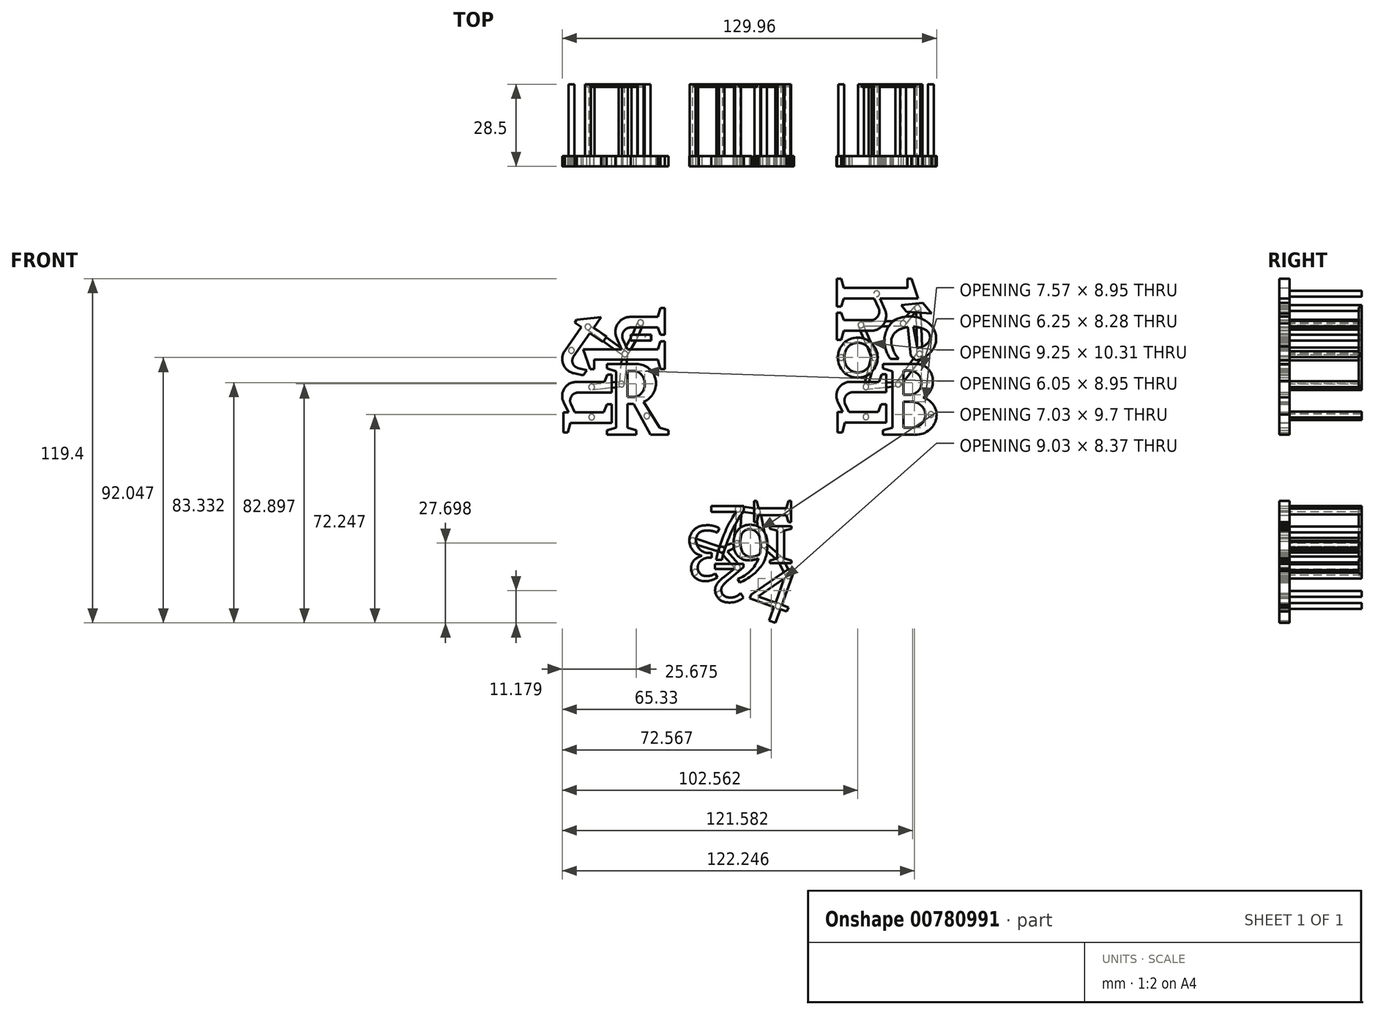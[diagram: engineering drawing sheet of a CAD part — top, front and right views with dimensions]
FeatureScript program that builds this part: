
annotation { "Feature Type Name" : "Feature", "Feature Type Description" : "" }
export const myFeature = defineFeature(function(context is Context, id is Id, definition is map)
    precondition{}
    {
        {
            var Q0;
            Q0=qCreatedBy(makeId("Front.planeOp"),FACE);
            var sketch = newSketch(context, id + "F0", { "sketchPlane" : qUnion([Q0])});
            skLineSegment(sketch, "E0", {"start": v(-78.02, 15.2) * mm, "end": v(-67.8, 15.2) * mm});
            skLineSegment(sketch, "E1", {"start": v(-67.8, 15.2) * mm, "end": v(-67.8, 16.73) * mm});
            skLineSegment(sketch, "E2", {"start": v(-67.8, 16.73) * mm, "end": v(-70.86, 17.67) * mm});
            skLineSegment(sketch, "E3", {"start": v(-70.86, 17.67) * mm, "end": v(-70.86, 25.9) * mm});
            skLineSegment(sketch, "E4", {"start": v(-70.86, 25.9) * mm, "end": v(-68.64, 25.9) * mm});
            skLineSegment(sketch, "E5", {"start": v(-68.64, 25.9) * mm, "end": v(-62.81, 15.2) * mm});
            skLineSegment(sketch, "E6", {"start": v(-62.81, 15.2) * mm, "end": v(-56.63, 15.2) * mm});
            skLineSegment(sketch, "E7", {"start": v(-56.63, 15.2) * mm, "end": v(-56.63, 16.73) * mm});
            skLineSegment(sketch, "E8", {"start": v(-56.63, 16.73) * mm, "end": v(-59.61, 17.67) * mm});
            skLineSegment(sketch, "E9", {"start": v(-59.61, 17.67) * mm, "end": v(-65.23, 26.62) * mm});
            skLineSegment(sketch, "E10", {"start": v(-78.02, 15.2) * mm, "end": v(-78.02, 16.73) * mm});
            skLineSegment(sketch, "E11", {"start": v(-78.02, 16.73) * mm, "end": v(-74.74, 17.67) * mm});
            skLineSegment(sketch, "E12", {"start": v(-74.74, 17.67) * mm, "end": v(-74.74, 37.23) * mm});
            skLineSegment(sketch, "E13", {"start": v(-74.74, 37.23) * mm, "end": v(-78.02, 38.21) * mm});
            skLineSegment(sketch, "E14", {"start": v(-78.02, 38.21) * mm, "end": v(-78.02, 39.74) * mm});
            skLineSegment(sketch, "E15", {"start": v(-78.02, 39.74) * mm, "end": v(-68.86, 39.74) * mm});
            skArc(sketch, "E16", {"start": v(-65.23, 26.62) * mm, "mid": v(-61.06, 34.23) * mm, "end": v(-67.76, 39.74) * mm});
            skArc(sketch, "E17", {"start": v(-67.74, 28.32) * mm, "mid": v(-64.81, 32.8) * mm, "end": v(-67.74, 37.27) * mm});
            skLineSegment(sketch, "E18", {"start": v(-67.74, 37.27) * mm, "end": v(-70.86, 37.27) * mm});
            skLineSegment(sketch, "E19", {"start": v(-70.86, 37.27) * mm, "end": v(-70.86, 28.32) * mm});
            skLineSegment(sketch, "E20", {"start": v(-70.86, 28.32) * mm, "end": v(-67.74, 28.32) * mm});
            skLineSegment(sketch, "E21", {"start": v(-68.86, 39.74) * mm, "end": v(-67.76, 39.74) * mm});
            skSolve(sketch);
        }
        {
            var Q0;
            Q0=makeQuery(id+"F0.imprint","IMPRINT",FACE,{"disambiguationData":[TD([[makeQuery(id+"F0.imprint","IMPRINT",EDGE,{"derivedFrom":sQuery(id+"F0.wireOp",EDGE,"E0")}),1.0]])]});
            extrude(context, id + "F1", {"entities" : qUnion([Q0]), "depth" : 3.5 * mm, "offsetDistance" : 25 * mm});
        }
        {
            var Q0;
            Q0=makeQuery(id+"F1.opExtrude","SWEPT_EDGE",EDGE,{"disambiguationData":[OSD([sQuery(id+"F0.wireOp",EDGE,"E17"),sQuery(id+"F0.wireOp",EDGE,"E18")])]});
            var Q1;
            Q1=makeQuery(id+"F1.opExtrude","SWEPT_EDGE",EDGE,{"disambiguationData":[OSD([sQuery(id+"F0.wireOp",EDGE,"E17"),sQuery(id+"F0.wireOp",EDGE,"E20")])]});
            fillet(context, id + "F2", {"entities" : qUnion([Q0, Q1]), "radius" : 3 * mm, "tangentPropagation" : true, "allowEdgeOverflow" : false});
        }
        {
            var Q0;
            Q0=qCreatedBy(makeId("Front.planeOp"),FACE);
            var sketch = newSketch(context, id + "F3", { "sketchPlane" : qUnion([Q0])});
            skLineSegment(sketch, "E22", {"start": v(-41.77, 15.2) * mm, "end": v(-34.7, 15.2) * mm});
            skLineSegment(sketch, "E23", {"start": v(-34.7, 15.2) * mm, "end": v(-34.7, 16.73) * mm});
            skLineSegment(sketch, "E24", {"start": v(-34.7, 16.73) * mm, "end": v(-38.08, 17.67) * mm});
            skLineSegment(sketch, "E25", {"start": v(-38.08, 17.67) * mm, "end": v(-38.08, 32) * mm});
            skLineSegment(sketch, "E26", {"start": v(-38.08, 32) * mm, "end": v(-44.47, 32) * mm});
            skLineSegment(sketch, "E27", {"start": v(-44.47, 32) * mm, "end": v(-44.47, 30.27) * mm});
            skLineSegment(sketch, "E28", {"start": v(-44.47, 30.27) * mm, "end": v(-41.77, 29.18) * mm});
            skLineSegment(sketch, "E29", {"start": v(-41.77, 29.18) * mm, "end": v(-41.77, 19.11) * mm});
            skLineSegment(sketch, "E30", {"start": v(-41.77, 15.2) * mm, "end": v(-41.77, 16.98) * mm});
            skLineSegment(sketch, "E31", {"start": v(-41.77, 16.98) * mm, "end": v(-45.17, 15.3) * mm});
            skLineSegment(sketch, "E32", {"start": v(-41.77, 19.11) * mm, "end": v(-44.76, 17.72) * mm});
            skLineSegment(sketch, "E33", {"start": v(-52.26, 19.48) * mm, "end": v(-52.26, 29.48) * mm});
            skLineSegment(sketch, "E34", {"start": v(-52.26, 29.48) * mm, "end": v(-54.82, 30.46) * mm});
            skLineSegment(sketch, "E35", {"start": v(-54.82, 30.46) * mm, "end": v(-54.82, 32) * mm});
            skLineSegment(sketch, "E36", {"start": v(-54.82, 32) * mm, "end": v(-48.6, 32) * mm});
            skLineSegment(sketch, "E37", {"start": v(-48.6, 32) * mm, "end": v(-48.6, 20.2) * mm});
            skArc(sketch, "E38", {"start": v(-52.26, 19.48) * mm, "mid": v(-49.87, 15.44) * mm, "end": v(-45.17, 15.3) * mm});
            skArc(sketch, "E39", {"start": v(-48.6, 20.2) * mm, "mid": v(-47.31, 17.98) * mm, "end": v(-44.76, 17.72) * mm});
            skSolve(sketch);
        }
        {
            var Q0;
            Q0=makeQuery(id+"F3.imprint","IMPRINT",FACE,{"disambiguationData":[TD([[makeQuery(id+"F3.imprint","IMPRINT",EDGE,{"derivedFrom":sQuery(id+"F3.wireOp",EDGE,"E22")}),1.0]])]});
            extrude(context, id + "F4", {"entities" : qUnion([Q0]), "depth" : 3.5 * mm, "offsetDistance" : 25 * mm});
        }
        {
            var Q0;
            Q0=qCreatedBy(makeId("Front.planeOp"),FACE);
            var sketch = newSketch(context, id + "F5", { "sketchPlane" : qUnion([Q0])});
            skLineSegment(sketch, "E40", {"start": v(-20.57, 32) * mm, "end": v(-26.02, 32) * mm});
            skLineSegment(sketch, "E41", {"start": v(-26.02, 32) * mm, "end": v(-26.02, 36.51) * mm});
            skLineSegment(sketch, "E42", {"start": v(-26.02, 36.51) * mm, "end": v(-32.46, 30.8) * mm});
            skLineSegment(sketch, "E43", {"start": v(-32.46, 30.8) * mm, "end": v(-32.46, 29.66) * mm});
            skLineSegment(sketch, "E44", {"start": v(-32.46, 29.66) * mm, "end": v(-29.69, 29.66) * mm});
            skLineSegment(sketch, "E45", {"start": v(-29.69, 29.66) * mm, "end": v(-29.69, 19.66) * mm});
            skLineSegment(sketch, "E46", {"start": v(-20.57, 32) * mm, "end": v(-20.57, 29.66) * mm});
            skLineSegment(sketch, "E47", {"start": v(-20.57, 29.66) * mm, "end": v(-26.02, 29.66) * mm});
            skLineSegment(sketch, "E48", {"start": v(-26.02, 29.66) * mm, "end": v(-26.02, 19.66) * mm});
            skLineSegment(sketch, "E49", {"start": v(-22.55, 17.37) * mm, "end": v(-19.53, 18.45) * mm});
            skLineSegment(sketch, "E50", {"start": v(-19.53, 18.45) * mm, "end": v(-19.53, 16.4) * mm});
            skLineSegment(sketch, "E51", {"start": v(-19.53, 16.4) * mm, "end": v(-22.56, 15.09) * mm});
            skArc(sketch, "E52", {"start": v(-29.69, 19.66) * mm, "mid": v(-27.34, 15.48) * mm, "end": v(-22.56, 15.09) * mm});
            skArc(sketch, "E53", {"start": v(-26.02, 19.66) * mm, "mid": v(-24.85, 17.65) * mm, "end": v(-22.55, 17.37) * mm});
            skSolve(sketch);
        }
        {
            var Q0;
            Q0=makeQuery(id+"F5.imprint","IMPRINT",FACE,{"disambiguationData":[TD([[makeQuery(id+"F5.imprint","IMPRINT",EDGE,{"derivedFrom":sQuery(id+"F5.wireOp",EDGE,"E40")}),1.0]])]});
            extrude(context, id + "F6", {"entities" : qUnion([Q0]), "depth" : 3.5 * mm, "offsetDistance" : 25 * mm});
        }
        {
            var Q0;
            Q0=qCreatedBy(makeId("Front.planeOp"),FACE);
            var sketch = newSketch(context, id + "F7", { "sketchPlane" : qUnion([Q0])});
            skLineSegment(sketch, "E54", {"start": v(-17.06, 15.2) * mm, "end": v(-7.42, 15.2) * mm});
            skLineSegment(sketch, "E55", {"start": v(-7.42, 15.2) * mm, "end": v(-7.42, 16.73) * mm});
            skLineSegment(sketch, "E56", {"start": v(-7.42, 16.73) * mm, "end": v(-10.26, 17.67) * mm});
            skLineSegment(sketch, "E57", {"start": v(-10.26, 17.67) * mm, "end": v(-10.26, 28.2) * mm});
            skLineSegment(sketch, "E58", {"start": v(-10.26, 28.2) * mm, "end": v(-6.9, 29.76) * mm});
            skLineSegment(sketch, "E59", {"start": v(-17.06, 15.2) * mm, "end": v(-17.06, 16.73) * mm});
            skLineSegment(sketch, "E60", {"start": v(-17.06, 16.73) * mm, "end": v(-13.88, 17.67) * mm});
            skLineSegment(sketch, "E61", {"start": v(-13.88, 17.67) * mm, "end": v(-13.88, 39.74) * mm});
            skLineSegment(sketch, "E62", {"start": v(-13.88, 39.74) * mm, "end": v(-17.06, 39.74) * mm});
            skLineSegment(sketch, "E63", {"start": v(-17.06, 39.74) * mm, "end": v(-17.06, 41.1) * mm});
            skLineSegment(sketch, "E64", {"start": v(-17.06, 41.1) * mm, "end": v(-10.26, 43.5) * mm});
            skLineSegment(sketch, "E65", {"start": v(-10.26, 43.5) * mm, "end": v(-10.26, 30.24) * mm});
            skLineSegment(sketch, "E66", {"start": v(-10.26, 30.24) * mm, "end": v(-6.4, 31.9) * mm});
            skLineSegment(sketch, "E67", {"start": v(-2.67, 27.17) * mm, "end": v(-2.67, 17.67) * mm});
            skLineSegment(sketch, "E68", {"start": v(-2.67, 17.67) * mm, "end": v(-5.22, 16.73) * mm});
            skLineSegment(sketch, "E69", {"start": v(-5.22, 16.73) * mm, "end": v(-5.22, 15.2) * mm});
            skLineSegment(sketch, "E70", {"start": v(-5.22, 15.2) * mm, "end": v(4.1, 15.2) * mm});
            skLineSegment(sketch, "E71", {"start": v(4.1, 15.2) * mm, "end": v(4.1, 16.73) * mm});
            skLineSegment(sketch, "E72", {"start": v(4.1, 16.73) * mm, "end": v(0.99, 17.67) * mm});
            skLineSegment(sketch, "E73", {"start": v(0.99, 17.67) * mm, "end": v(0.99, 27.07) * mm});
            skArc(sketch, "E74", {"start": v(0.99, 27.07) * mm, "mid": v(-1.37, 31.53) * mm, "end": v(-6.4, 31.9) * mm});
            skArc(sketch, "E75", {"start": v(-2.67, 27.17) * mm, "mid": v(-4.12, 29.56) * mm, "end": v(-6.9, 29.76) * mm});
            skSolve(sketch);
        }
        {
            var Q0;
            Q0=makeQuery(id+"F7.imprint","IMPRINT",FACE,{"disambiguationData":[TD([[makeQuery(id+"F7.imprint","IMPRINT",EDGE,{"derivedFrom":sQuery(id+"F7.wireOp",EDGE,"E54")}),1.0]])]});
            extrude(context, id + "F8", {"entities" : qUnion([Q0]), "depth" : 3.5 * mm, "offsetDistance" : 25 * mm});
        }
        {
            var Q0;
            Q0=qCreatedBy(makeId("Front.planeOp"),FACE);
            var sketch = newSketch(context, id + "F9", { "sketchPlane" : qUnion([Q0])});
            skLineSegment(sketch, "E76", {"start": v(29.79, 15.2) * mm, "end": v(17.79, 15.2) * mm});
            skLineSegment(sketch, "E77", {"start": v(17.79, 15.2) * mm, "end": v(17.79, 16.73) * mm});
            skLineSegment(sketch, "E78", {"start": v(17.79, 16.73) * mm, "end": v(21.07, 17.67) * mm});
            skLineSegment(sketch, "E79", {"start": v(21.07, 17.67) * mm, "end": v(21.07, 37.23) * mm});
            skLineSegment(sketch, "E80", {"start": v(21.07, 37.23) * mm, "end": v(17.79, 38.21) * mm});
            skLineSegment(sketch, "E81", {"start": v(17.79, 38.21) * mm, "end": v(17.79, 39.74) * mm});
            skLineSegment(sketch, "E82", {"start": v(17.79, 39.74) * mm, "end": v(29.42, 39.74) * mm});
            skLineSegment(sketch, "E83", {"start": v(27.65, 37.37) * mm, "end": v(24.95, 37.37) * mm});
            skLineSegment(sketch, "E84", {"start": v(24.95, 37.37) * mm, "end": v(24.95, 29.1) * mm});
            skLineSegment(sketch, "E85", {"start": v(24.95, 29.1) * mm, "end": v(27.65, 29.1) * mm});
            skLineSegment(sketch, "E86", {"start": v(27.84, 26.62) * mm, "end": v(24.95, 26.62) * mm});
            skLineSegment(sketch, "E87", {"start": v(24.95, 26.62) * mm, "end": v(24.95, 17.67) * mm});
            skLineSegment(sketch, "E88", {"start": v(24.95, 17.67) * mm, "end": v(28.14, 17.67) * mm});
            skArc(sketch, "E89", {"start": v(35.13, 33.82) * mm, "mid": v(33.53, 38) * mm, "end": v(29.42, 39.74) * mm});
            skArc(sketch, "E90", {"start": v(31.72, 28.11) * mm, "mid": v(34.29, 30.45) * mm, "end": v(35.13, 33.82) * mm});
            skArc(sketch, "E91", {"start": v(36.45, 22.2) * mm, "mid": v(35.03, 25.92) * mm, "end": v(31.72, 28.11) * mm});
            skArc(sketch, "E92", {"start": v(29.79, 15.2) * mm, "mid": v(34.49, 17.4) * mm, "end": v(36.45, 22.2) * mm});
            skArc(sketch, "E93", {"start": v(32.52, 22.31) * mm, "mid": v(31.02, 25.38) * mm, "end": v(27.84, 26.62) * mm});
            skArc(sketch, "E94", {"start": v(28.14, 17.67) * mm, "mid": v(31.33, 19.05) * mm, "end": v(32.52, 22.31) * mm});
            skArc(sketch, "E95", {"start": v(27.65, 29.1) * mm, "mid": v(31.2, 33.23) * mm, "end": v(27.65, 37.37) * mm});
            skSolve(sketch);
        }
        {
            var Q0;
            Q0=makeQuery(id+"F9.imprint","IMPRINT",FACE,{"disambiguationData":[TD([[makeQuery(id+"F9.imprint","IMPRINT",EDGE,{"derivedFrom":sQuery(id+"F9.wireOp",EDGE,"E76")}),-1.0]])]});
            extrude(context, id + "F10", {"entities" : qUnion([Q0]), "depth" : 3.5 * mm, "offsetDistance" : 25 * mm});
        }
        {
            var Q0;
            Q0=makeQuery(id+"F10.opExtrude","SWEPT_EDGE",EDGE,{"disambiguationData":[OSD([sQuery(id+"F9.wireOp",EDGE,"E83"),sQuery(id+"F9.wireOp",EDGE,"E95")])]});
            var Q1;
            Q1=makeQuery(id+"F10.opExtrude","SWEPT_EDGE",EDGE,{"disambiguationData":[OSD([sQuery(id+"F9.wireOp",EDGE,"E85"),sQuery(id+"F9.wireOp",EDGE,"E95")])]});
            fillet(context, id + "F11", {"entities" : qUnion([Q0, Q1]), "radius" : 3 * mm, "tangentPropagation" : true, "allowEdgeOverflow" : false});
        }
        {
            var Q0;
            Q0=qCreatedBy(makeId("Front.planeOp"),FACE);
            var sketch = newSketch(context, id + "F12", { "sketchPlane" : qUnion([Q0])});
            skLineSegment(sketch, "E96", {"start": v(90.8, 34.88) * mm, "end": v(93.74, 34.88) * mm});
            skLineSegment(sketch, "E97", {"start": v(93.74, 34.88) * mm, "end": v(99.81, 41.18) * mm});
            skLineSegment(sketch, "E98", {"start": v(99.81, 41.18) * mm, "end": v(95.06, 41.18) * mm});
            skLineSegment(sketch, "E99", {"start": v(95.06, 41.18) * mm, "end": v(90.8, 34.88) * mm});
            skLineSegment(sketch, "E100", {"start": v(99.7, 23.95) * mm, "end": v(101.36, 25.66) * mm});
            skArc(sketch, "E101", {"start": v(101.36, 25.66) * mm, "mid": v(99.76, 29.5) * mm, "end": v(96.55, 32.12) * mm});
            skArc(sketch, "E102", {"start": v(96.55, 32.12) * mm, "mid": v(92.2, 32.52) * mm, "end": v(88.49, 30.24) * mm});
            skArc(sketch, "E103", {"start": v(88.49, 30.24) * mm, "mid": v(86.13, 24.18) * mm, "end": v(87.72, 17.87) * mm});
            skArc(sketch, "E104", {"start": v(87.72, 17.87) * mm, "mid": v(91.03, 15.46) * mm, "end": v(95.06, 14.72) * mm});
            skArc(sketch, "E105", {"start": v(95.06, 14.72) * mm, "mid": v(98.1, 15.4) * mm, "end": v(100.86, 16.82) * mm});
            skLineSegment(sketch, "E106", {"start": v(100.86, 16.82) * mm, "end": v(100.86, 19.7) * mm});
            skArc(sketch, "E107", {"start": v(94.95, 17.1) * mm, "mid": v(98.11, 17.92) * mm, "end": v(100.86, 19.7) * mm});
            skArc(sketch, "E108", {"start": v(90.8, 19.7) * mm, "mid": v(92.53, 17.83) * mm, "end": v(94.95, 17.1) * mm});
            skArc(sketch, "E109", {"start": v(90.8, 29.14) * mm, "mid": v(89.98, 26.84) * mm, "end": v(89.7, 24.42) * mm});
            skArc(sketch, "E110", {"start": v(95.94, 29.14) * mm, "mid": v(93.38, 30.56) * mm, "end": v(90.8, 29.14) * mm});
            skArc(sketch, "E111", {"start": v(97.1, 26.21) * mm, "mid": v(96.68, 27.74) * mm, "end": v(95.94, 29.14) * mm});
            skLineSegment(sketch, "E112", {"start": v(99.7, 23.95) * mm, "end": v(89.81, 22.85) * mm});
            skLineSegment(sketch, "E113", {"start": v(97.1, 26.21) * mm, "end": v(89.7, 24.76) * mm});
            skPoint(sketch, "E113.endSnap0", {"position": v(89.7, 24.42) * mm});
            skArc(sketch, "E114.trimOffspring", {"start": v(89.81, 22.85) * mm, "mid": v(90.19, 21.23) * mm, "end": v(90.8, 19.7) * mm});
            skPoint(sketch, "E115.orphan", {"position": v(87.94, 24.42) * mm});
            skSolve(sketch);
        }
        {
            var Q0;
            Q0=makeQuery(id+"F12.imprint","IMPRINT",FACE,{"disambiguationData":[TD([[makeQuery(id+"F12.imprint","IMPRINT",EDGE,{"derivedFrom":sQuery(id+"F12.wireOp",EDGE,"E100")}),1.0]])]});
            var Q1;
            Q1=makeQuery(id+"F12.imprint","IMPRINT",FACE,{"disambiguationData":[TD([[makeQuery(id+"F12.imprint","IMPRINT",EDGE,{"derivedFrom":sQuery(id+"F12.wireOp",EDGE,"E96")}),1.0]])]});
            extrude(context, id + "F13", {"entities" : qUnion([Q0, Q1]), "depth" : 3.5 * mm, "offsetDistance" : 25 * mm});
        }
        {
            var Q0;
            Q0=makeQuery(id+"F4.opExtrude","SWEPT_BODY",BODY,{"disambiguationData":[OSD([sQuery(id+"F3.wireOp",EDGE,"E22"),sQuery(id+"F3.wireOp",EDGE,"E23"),sQuery(id+"F3.wireOp",EDGE,"E24"),sQuery(id+"F3.wireOp",EDGE,"E25"),sQuery(id+"F3.wireOp",EDGE,"E26"),sQuery(id+"F3.wireOp",EDGE,"E27"),sQuery(id+"F3.wireOp",EDGE,"E28"),sQuery(id+"F3.wireOp",EDGE,"E29"),sQuery(id+"F3.wireOp",EDGE,"E30"),sQuery(id+"F3.wireOp",EDGE,"E31"),sQuery(id+"F3.wireOp",EDGE,"E32"),sQuery(id+"F3.wireOp",EDGE,"E33"),sQuery(id+"F3.wireOp",EDGE,"E34"),sQuery(id+"F3.wireOp",EDGE,"E35"),sQuery(id+"F3.wireOp",EDGE,"E36"),sQuery(id+"F3.wireOp",EDGE,"E37"),sQuery(id+"F3.wireOp",EDGE,"E38"),sQuery(id+"F3.wireOp",EDGE,"E39")])]});
            transform(context, id + "F14", {"entities" : qUnion([Q0]), "transformType" : TransformType.TRANSLATION_3D, "dx" : 94.3 * mm, "dy" : 0 * mm, "dz" : 0 * mm, "makeCopy" : true});
        }
        {
            var Q0;
            Q0=makeQuery(id+"F8.opExtrude","SWEPT_BODY",BODY,{"disambiguationData":[OSD([sQuery(id+"F7.wireOp",EDGE,"E54"),sQuery(id+"F7.wireOp",EDGE,"E55"),sQuery(id+"F7.wireOp",EDGE,"E56"),sQuery(id+"F7.wireOp",EDGE,"E57"),sQuery(id+"F7.wireOp",EDGE,"E58"),sQuery(id+"F7.wireOp",EDGE,"E59"),sQuery(id+"F7.wireOp",EDGE,"E60"),sQuery(id+"F7.wireOp",EDGE,"E61"),sQuery(id+"F7.wireOp",EDGE,"E62"),sQuery(id+"F7.wireOp",EDGE,"E63"),sQuery(id+"F7.wireOp",EDGE,"E64"),sQuery(id+"F7.wireOp",EDGE,"E65"),sQuery(id+"F7.wireOp",EDGE,"E66"),sQuery(id+"F7.wireOp",EDGE,"E67"),sQuery(id+"F7.wireOp",EDGE,"E68"),sQuery(id+"F7.wireOp",EDGE,"E69"),sQuery(id+"F7.wireOp",EDGE,"E70"),sQuery(id+"F7.wireOp",EDGE,"E71"),sQuery(id+"F7.wireOp",EDGE,"E72"),sQuery(id+"F7.wireOp",EDGE,"E73"),sQuery(id+"F7.wireOp",EDGE,"E74"),sQuery(id+"F7.wireOp",EDGE,"E75")])]});
            transform(context, id + "F15", {"entities" : qUnion([Q0]), "transformType" : TransformType.TRANSLATION_3D, "dx" : 79.7 * mm, "dy" : 0 * mm, "dz" : 0 * mm, "makeCopy" : true});
        }
        {
            var Q0;
            Q0=qCreatedBy(makeId("Front.planeOp"),FACE);
            var sketch = newSketch(context, id + "F16", { "sketchPlane" : qUnion([Q0])});
            skLineSegment(sketch, "E116", {"start": v(-44.04, -29.35) * mm, "end": v(-36.6, -29.35) * mm});
            skLineSegment(sketch, "E117", {"start": v(-36.6, -29.35) * mm, "end": v(-36.6, -28.47) * mm});
            skLineSegment(sketch, "E118", {"start": v(-36.6, -28.47) * mm, "end": v(-39.1, -27.72) * mm});
            skLineSegment(sketch, "E119", {"start": v(-39.1, -27.72) * mm, "end": v(-39.1, -18.13) * mm});
            skLineSegment(sketch, "E120", {"start": v(-39.1, -18.13) * mm, "end": v(-36.6, -17.38) * mm});
            skLineSegment(sketch, "E121", {"start": v(-36.6, -17.38) * mm, "end": v(-36.6, -16.5) * mm});
            skLineSegment(sketch, "E122", {"start": v(-36.6, -16.5) * mm, "end": v(-44.04, -16.5) * mm});
            skLineSegment(sketch, "E123", {"start": v(-44.04, -16.5) * mm, "end": v(-44.04, -17.38) * mm});
            skLineSegment(sketch, "E124", {"start": v(-44.04, -17.38) * mm, "end": v(-41.53, -18.13) * mm});
            skLineSegment(sketch, "E125", {"start": v(-41.53, -18.13) * mm, "end": v(-41.53, -27.72) * mm});
            skLineSegment(sketch, "E126", {"start": v(-41.53, -27.72) * mm, "end": v(-44.04, -28.47) * mm});
            skLineSegment(sketch, "E127", {"start": v(-44.04, -28.47) * mm, "end": v(-44.04, -29.35) * mm});
            skSolve(sketch);
        }
        {
            var Q0;
            Q0=makeQuery(id+"F16.imprint","IMPRINT",FACE,{"disambiguationData":[TD([[makeQuery(id+"F16.imprint","IMPRINT",EDGE,{"derivedFrom":sQuery(id+"F16.wireOp",EDGE,"E116")}),1.0]])]});
            extrude(context, id + "F17", {"entities" : qUnion([Q0]), "depth" : 3.5 * mm, "offsetDistance" : 25 * mm});
        }
        {
            var Q0;
            Q0=makeQuery(id+"F17.opExtrude","SWEPT_BODY",BODY,{"disambiguationData":[OSD([sQuery(id+"F16.wireOp",EDGE,"E116"),sQuery(id+"F16.wireOp",EDGE,"E117"),sQuery(id+"F16.wireOp",EDGE,"E118"),sQuery(id+"F16.wireOp",EDGE,"E119"),sQuery(id+"F16.wireOp",EDGE,"E120"),sQuery(id+"F16.wireOp",EDGE,"E121"),sQuery(id+"F16.wireOp",EDGE,"E122"),sQuery(id+"F16.wireOp",EDGE,"E123"),sQuery(id+"F16.wireOp",EDGE,"E124"),sQuery(id+"F16.wireOp",EDGE,"E125"),sQuery(id+"F16.wireOp",EDGE,"E126"),sQuery(id+"F16.wireOp",EDGE,"E127")])]});
            transform(context, id + "F18", {"entities" : qUnion([Q0]), "transformType" : TransformType.TRANSLATION_3D, "dx" : 104.3 * mm, "dy" : 0 * mm, "dz" : 0 * mm, "makeCopy" : true});
        }
        {
            var Q0;
            Q0=qCreatedBy(makeId("Front.planeOp"),FACE);
            var sketch = newSketch(context, id + "F19", { "sketchPlane" : qUnion([Q0])});
            skLineSegment(sketch, "E128", {"start": v(3.98, -15.35) * mm, "end": v(3.98, -27.8) * mm});
            skLineSegment(sketch, "E129", {"start": v(3.98, -34.4) * mm, "end": v(1.63, -34.4) * mm});
            skLineSegment(sketch, "E130", {"start": v(1.63, -34.4) * mm, "end": v(1.63, -29.38) * mm});
            skLineSegment(sketch, "E131", {"start": v(1.63, -18.9) * mm, "end": v(-4.74, -27.8) * mm});
            skLineSegment(sketch, "E132", {"start": v(-4.74, -27.8) * mm, "end": v(1.63, -27.8) * mm});
            skLineSegment(sketch, "E133", {"start": v(6.36, -27.8) * mm, "end": v(6.36, -29.38) * mm});
            skLineSegment(sketch, "E134", {"start": v(6.36, -29.38) * mm, "end": v(3.98, -29.38) * mm});
            skLineSegment(sketch, "E135", {"start": v(-7.27, -29.38) * mm, "end": v(-7.27, -28.07) * mm});
            skLineSegment(sketch, "E136", {"start": v(-7.27, -28.07) * mm, "end": v(1.83, -15.35) * mm});
            skLineSegment(sketch, "E137", {"start": v(1.83, -15.35) * mm, "end": v(3.98, -15.35) * mm});
            skLineSegment(sketch, "E138.trimOffspring", {"start": v(3.98, -27.8) * mm, "end": v(6.36, -27.8) * mm});
            skLineSegment(sketch, "E139.trimOffspring", {"start": v(1.63, -29.38) * mm, "end": v(-7.27, -29.38) * mm});
            skLineSegment(sketch, "E140.trimOffspring", {"start": v(1.63, -27.8) * mm, "end": v(1.63, -18.9) * mm});
            skLineSegment(sketch, "E141.trimOffspring", {"start": v(3.98, -29.38) * mm, "end": v(3.98, -34.4) * mm});
            skSolve(sketch);
        }
        {
            var Q0;
            Q0=makeQuery(id+"F19.imprint","IMPRINT",FACE,{"disambiguationData":[TD([[makeQuery(id+"F19.imprint","IMPRINT",EDGE,{"derivedFrom":sQuery(id+"F19.wireOp",EDGE,"E128")}),-1.0]])]});
            extrude(context, id + "F20", {"entities" : qUnion([Q0]), "depth" : 3.5 * mm, "offsetDistance" : 25 * mm});
        }
        {
            var Q0;
            Q0=qCreatedBy(makeId("Front.planeOp"),FACE);
            var sketch = newSketch(context, id + "F21", { "sketchPlane" : qUnion([Q0])});
            skLineSegment(sketch, "E142", {"start": v(77.45, -18.55) * mm, "end": v(68.9, -18.55) * mm});
            skLineSegment(sketch, "E143", {"start": v(68.9, -18.55) * mm, "end": v(68.9, -16.5) * mm});
            skLineSegment(sketch, "E144", {"start": v(68.9, -16.5) * mm, "end": v(80.12, -16.5) * mm});
            skLineSegment(sketch, "E145", {"start": v(80.12, -16.5) * mm, "end": v(80.12, -18.07) * mm});
            skLineSegment(sketch, "E146", {"start": v(70.5, -35.3) * mm, "end": v(72.5, -35.3) * mm});
            skArc(sketch, "E147", {"start": v(77.45, -18.55) * mm, "mid": v(73.16, -26.58) * mm, "end": v(70.5, -35.3) * mm});
            skArc(sketch, "E148", {"start": v(80.12, -18.07) * mm, "mid": v(75.5, -26.32) * mm, "end": v(72.5, -35.3) * mm});
            skSolve(sketch);
        }
        {
            var Q0;
            Q0=makeQuery(id+"F21.imprint","IMPRINT",FACE,{"disambiguationData":[TD([[makeQuery(id+"F21.imprint","IMPRINT",EDGE,{"derivedFrom":sQuery(id+"F21.wireOp",EDGE,"E142")}),-1.0]])]});
            extrude(context, id + "F22", {"entities" : qUnion([Q0]), "depth" : 3.5 * mm, "offsetDistance" : 25 * mm});
        }
        {
            var Q0;
            Q0=qCreatedBy(makeId("Front.planeOp"),FACE);
            var sketch = newSketch(context, id + "F23", { "sketchPlane" : qUnion([Q0])});
            skCircle(sketch, "E149", {"center": v(51.05, -22.75) * mm, "radius": 6.94 * mm});
            skPoint(sketch, "E149.first.point", {"position": v(51, -15.8) * mm});
            skPoint(sketch, "E149.second.point", {"position": v(45.69, -27.17) * mm});
            skPoint(sketch, "E149.third.point", {"position": v(55.6, -28) * mm});
            skArc(sketch, "E150", {"start": v(55.13, -20.1) * mm, "mid": v(51.07, -17.6) * mm, "end": v(47, -20.1) * mm});
            skArc(sketch, "E151", {"start": v(55.13, -25.4) * mm, "mid": v(55.68, -22.75) * mm, "end": v(55.13, -20.1) * mm});
            skArc(sketch, "E152", {"start": v(47, -25.4) * mm, "mid": v(51.07, -27.9) * mm, "end": v(55.13, -25.4) * mm});
            skArc(sketch, "E153", {"start": v(47, -20.1) * mm, "mid": v(46.43, -22.75) * mm, "end": v(47, -25.4) * mm});
            skSolve(sketch);
        }
        {
            var Q0;
            Q0=makeQuery(id+"F23.imprint","IMPRINT",FACE,{"disambiguationData":[TD([[makeQuery(id+"F23.imprint","IMPRINT",EDGE,{"derivedFrom":sQuery(id+"F23.wireOp",EDGE,"E149")}),1.0]])]});
            extrude(context, id + "F24", {"entities" : qUnion([Q0]), "depth" : 3.5 * mm, "offsetDistance" : 25 * mm});
        }
        {
            var Q0;
            Q0=qCreatedBy(makeId("Front.planeOp"),FACE);
            var sketch = newSketch(context, id + "F25", { "sketchPlane" : qUnion([Q0])});
            skLineSegment(sketch, "E154", {"start": v(-32.6, -34.83) * mm, "end": v(-31.92, -36.07) * mm});
            skArc(sketch, "E155", {"start": v(-31.92, -36.07) * mm, "mid": v(-27.4, -33.47) * mm, "end": v(-23.88, -29.64) * mm});
            skArc(sketch, "E156", {"start": v(-23.88, -29.64) * mm, "mid": v(-22.4, -25.11) * mm, "end": v(-22.58, -20.35) * mm});
            skArc(sketch, "E157", {"start": v(-22.58, -20.35) * mm, "mid": v(-24.48, -17.39) * mm, "end": v(-27.75, -16.08) * mm});
            skArc(sketch, "E158", {"start": v(-27.75, -16.08) * mm, "mid": v(-31.59, -17.06) * mm, "end": v(-33.8, -20.35) * mm});
            skArc(sketch, "E159", {"start": v(-33.8, -20.35) * mm, "mid": v(-34.09, -22.6) * mm, "end": v(-33.8, -24.86) * mm});
            skArc(sketch, "E160", {"start": v(-33.8, -24.86) * mm, "mid": v(-32.49, -26.9) * mm, "end": v(-30.42, -28.18) * mm});
            skArc(sketch, "E161", {"start": v(-30.42, -28.18) * mm, "mid": v(-27.86, -28.35) * mm, "end": v(-25.36, -27.73) * mm});
            skArc(sketch, "E162", {"start": v(-32.6, -34.83) * mm, "mid": v(-28.19, -32.08) * mm, "end": v(-25.36, -27.73) * mm});
            skArc(sketch, "E163", {"start": v(-24.9, -26.21) * mm, "mid": v(-24.66, -23.55) * mm, "end": v(-24.9, -20.88) * mm});
            skArc(sketch, "E164", {"start": v(-24.9, -20.88) * mm, "mid": v(-25.91, -18.76) * mm, "end": v(-27.94, -17.58) * mm});
            skPoint(sketch, "E165", {"position": v(-34.09, -22.6) * mm});
            skPoint(sketch, "E166", {"position": v(-31.68, -22.64) * mm});
            skArc(sketch, "E167", {"start": v(-27.94, -17.58) * mm, "mid": v(-30, -18) * mm, "end": v(-31.34, -19.63) * mm});
            skArc(sketch, "E168", {"start": v(-31.34, -19.63) * mm, "mid": v(-31.68, -22.61) * mm, "end": v(-30.95, -25.53) * mm});
            skArc(sketch, "E169", {"start": v(-30.95, -25.53) * mm, "mid": v(-29.66, -26.77) * mm, "end": v(-27.94, -27.25) * mm});
            skArc(sketch, "E170", {"start": v(-27.94, -27.25) * mm, "mid": v(-26.37, -26.95) * mm, "end": v(-24.92, -26.27) * mm});
            skArc(sketch, "E171.trimOffspring", {"start": v(-24.92, -26.27) * mm, "mid": v(-24.91, -26.24) * mm, "end": v(-24.9, -26.21) * mm});
            skPoint(sketch, "E172.orphan", {"position": v(-23.96, -25.53) * mm});
            skSolve(sketch);
        }
        {
            var Q0;
            Q0=makeQuery(id+"F25.imprint","IMPRINT",FACE,{"disambiguationData":[TD([[makeQuery(id+"F25.imprint","IMPRINT",EDGE,{"derivedFrom":sQuery(id+"F25.wireOp",EDGE,"E154")}),1.0]])]});
            extrude(context, id + "F26", {"entities" : qUnion([Q0]), "depth" : 3.5 * mm, "offsetDistance" : 25 * mm});
        }
        {
            var Q0;
            Q0=qCreatedBy(makeId("Front.planeOp"),FACE);
            var sketch = newSketch(context, id + "F27", { "sketchPlane" : qUnion([Q0])});
            skLineSegment(sketch, "E173", {"start": v(-19.06, -17.35) * mm, "end": v(-18.22, -18.65) * mm});
            skLineSegment(sketch, "E174", {"start": v(-17.14, -24.16) * mm, "end": v(-17.14, -25.79) * mm});
            skLineSegment(sketch, "E175", {"start": v(-19.06, -32.87) * mm, "end": v(-19.75, -34.37) * mm});
            skArc(sketch, "E176", {"start": v(-12.61, -16.41) * mm, "mid": v(-15.95, -16.09) * mm, "end": v(-19.06, -17.35) * mm});
            skArc(sketch, "E177", {"start": v(-10.6, -22.78) * mm, "mid": v(-10.12, -19.12) * mm, "end": v(-12.61, -16.41) * mm});
            skArc(sketch, "E178", {"start": v(-13.75, -24.8) * mm, "mid": v(-11.98, -24.08) * mm, "end": v(-10.6, -22.78) * mm});
            skArc(sketch, "E179", {"start": v(-19.75, -34.37) * mm, "mid": v(-16.24, -35.41) * mm, "end": v(-12.61, -34.9) * mm});
            skArc(sketch, "E180", {"start": v(-12.61, -34.9) * mm, "mid": v(-9.5, -31.3) * mm, "end": v(-10.6, -26.67) * mm});
            skArc(sketch, "E181", {"start": v(-10.6, -26.67) * mm, "mid": v(-12, -25.43) * mm, "end": v(-13.75, -24.8) * mm});
            skArc(sketch, "E182", {"start": v(-13.75, -18.1) * mm, "mid": v(-16.05, -17.8) * mm, "end": v(-18.22, -18.65) * mm});
            skArc(sketch, "E183", {"start": v(-13.75, -23.42) * mm, "mid": v(-12.26, -20.76) * mm, "end": v(-13.75, -18.1) * mm});
            skLineSegment(sketch, "E184", {"start": v(-17.14, -24.16) * mm, "end": v(-16.1, -24.16) * mm});
            skLineSegment(sketch, "E185", {"start": v(-17.14, -25.79) * mm, "end": v(-16.1, -25.79) * mm});
            skArc(sketch, "E186", {"start": v(-16.1, -24.16) * mm, "mid": v(-14.87, -23.97) * mm, "end": v(-13.75, -23.42) * mm});
            skArc(sketch, "E187", {"start": v(-11.68, -29.94) * mm, "mid": v(-13.07, -26.99) * mm, "end": v(-16.1, -25.79) * mm});
            skArc(sketch, "E188", {"start": v(-19.06, -32.87) * mm, "mid": v(-16.72, -33.52) * mm, "end": v(-14.29, -33.48) * mm});
            skArc(sketch, "E189", {"start": v(-14.29, -33.48) * mm, "mid": v(-12.26, -32.25) * mm, "end": v(-11.68, -29.94) * mm});
            skSolve(sketch);
        }
        {
            var Q0;
            Q0=makeQuery(id+"F27.imprint","IMPRINT",FACE,{"disambiguationData":[TD([[makeQuery(id+"F27.imprint","IMPRINT",EDGE,{"derivedFrom":sQuery(id+"F27.wireOp",EDGE,"E173")}),1.0]])]});
            extrude(context, id + "F28", {"entities" : qUnion([Q0]), "depth" : 3.5 * mm, "offsetDistance" : 25 * mm});
        }
        {
            var Q0;
            Q0=qCreatedBy(makeId("Front.planeOp"),FACE);
            var sketch = newSketch(context, id + "F29", { "sketchPlane" : qUnion([Q0])});
            skLineSegment(sketch, "E190.bottom", {"start": v(14.61, -21.22) * mm, "end": v(21.72, -21.22) * mm});
            skLineSegment(sketch, "E190.top", {"start": v(14.61, -23.3) * mm, "end": v(21.72, -23.3) * mm});
            skLineSegment(sketch, "E190.left", {"start": v(14.61, -21.22) * mm, "end": v(14.61, -23.3) * mm});
            skLineSegment(sketch, "E190.right", {"start": v(21.72, -21.22) * mm, "end": v(21.72, -23.3) * mm});
            skSolve(sketch);
        }
        {
            var Q0;
            Q0=makeQuery(id+"F29.imprint","IMPRINT",FACE,{"disambiguationData":[TD([[makeQuery(id+"F29.imprint","IMPRINT",EDGE,{"derivedFrom":sQuery(id+"F29.wireOp",EDGE,"E190.bottom")}),-1.0]])]});
            extrude(context, id + "F30", {"entities" : qUnion([Q0]), "depth" : 3.5 * mm, "offsetDistance" : 25 * mm});
        }
        {
            var Q0;
            Q0=qCreatedBy(makeId("Front.planeOp"),FACE);
            var sketch = newSketch(context, id + "F31", { "sketchPlane" : qUnion([Q0])});
            skLineSegment(sketch, "E191", {"start": v(31.67, -28.2) * mm, "end": v(31.67, -29.34) * mm});
            skLineSegment(sketch, "E192", {"start": v(31.67, -29.34) * mm, "end": v(41.55, -29.34) * mm});
            skLineSegment(sketch, "E193", {"start": v(41.55, -29.34) * mm, "end": v(41.55, -27.55) * mm});
            skLineSegment(sketch, "E194", {"start": v(41.55, -27.55) * mm, "end": v(35.03, -27.55) * mm});
            skLineSegment(sketch, "E195", {"start": v(31.63, -17.67) * mm, "end": v(32.7, -19.2) * mm});
            skLineSegment(sketch, "E196", {"start": v(31.67, -28.2) * mm, "end": v(36.88, -23.82) * mm});
            skLineSegment(sketch, "E197", {"start": v(35.03, -27.55) * mm, "end": v(38.33, -24.95) * mm});
            skArc(sketch, "E198", {"start": v(41.22, -22.06) * mm, "mid": v(41.06, -18.32) * mm, "end": v(38.05, -16.08) * mm});
            skArc(sketch, "E199", {"start": v(39.1, -21.51) * mm, "mid": v(39.18, -19.3) * mm, "end": v(37.5, -17.84) * mm});
            skArc(sketch, "E200", {"start": v(38.05, -16.08) * mm, "mid": v(34.67, -16.17) * mm, "end": v(31.63, -17.67) * mm});
            skArc(sketch, "E201", {"start": v(38.33, -24.95) * mm, "mid": v(39.86, -23.59) * mm, "end": v(41.22, -22.06) * mm});
            skArc(sketch, "E202", {"start": v(36.88, -23.82) * mm, "mid": v(38.06, -22.72) * mm, "end": v(39.1, -21.51) * mm});
            skArc(sketch, "E203", {"start": v(37.5, -17.84) * mm, "mid": v(34.92, -17.84) * mm, "end": v(32.7, -19.2) * mm});
            skSolve(sketch);
        }
        {
            var Q0;
            Q0=makeQuery(id+"F31.imprint","IMPRINT",FACE,{"disambiguationData":[TD([[makeQuery(id+"F31.imprint","IMPRINT",EDGE,{"derivedFrom":sQuery(id+"F31.wireOp",EDGE,"E191")}),1.0]])]});
            extrude(context, id + "F32", {"entities" : qUnion([Q0]), "depth" : 3.5 * mm, "offsetDistance" : 25 * mm});
        }
        {
            var Q0;
            Q0=makeQuery(id+"F32.opExtrude","SWEPT_EDGE",EDGE,{"disambiguationData":[OSD([sQuery(id+"F31.wireOp",EDGE,"E198"),sQuery(id+"F31.wireOp",EDGE,"E201")])]});
            fillet(context, id + "F33", {"entities" : qUnion([Q0]), "radius" : 4 * mm, "tangentPropagation" : true, "allowEdgeOverflow" : false});
        }
        {
            var Q0;
            Q0=makeQuery(id+"F32.opExtrude","SWEPT_EDGE",EDGE,{"disambiguationData":[OSD([sQuery(id+"F31.wireOp",EDGE,"E199"),sQuery(id+"F31.wireOp",EDGE,"E202")])]});
            fillet(context, id + "F34", {"entities" : qUnion([Q0]), "radius" : 2.12 * mm, "tangentPropagation" : true, "allowEdgeOverflow" : false});
        }
        {
            var Q0;
            Q0=makeQuery(id+"F1.opExtrude","CAP_FACE",FACE,{"disambiguationData":[OSD([sQuery(id+"F0.wireOp",EDGE,"E0"),sQuery(id+"F0.wireOp",EDGE,"E1"),sQuery(id+"F0.wireOp",EDGE,"E2"),sQuery(id+"F0.wireOp",EDGE,"E3"),sQuery(id+"F0.wireOp",EDGE,"E4"),sQuery(id+"F0.wireOp",EDGE,"E5"),sQuery(id+"F0.wireOp",EDGE,"E6"),sQuery(id+"F0.wireOp",EDGE,"E7"),sQuery(id+"F0.wireOp",EDGE,"E8"),sQuery(id+"F0.wireOp",EDGE,"E9"),sQuery(id+"F0.wireOp",EDGE,"E10"),sQuery(id+"F0.wireOp",EDGE,"E11"),sQuery(id+"F0.wireOp",EDGE,"E12"),sQuery(id+"F0.wireOp",EDGE,"E13"),sQuery(id+"F0.wireOp",EDGE,"E14"),sQuery(id+"F0.wireOp",EDGE,"E15"),sQuery(id+"F0.wireOp",EDGE,"E16"),sQuery(id+"F0.wireOp",EDGE,"E17"),sQuery(id+"F0.wireOp",EDGE,"E18"),sQuery(id+"F0.wireOp",EDGE,"E19"),sQuery(id+"F0.wireOp",EDGE,"E20"),sQuery(id+"F0.wireOp",EDGE,"E21")])],"isStart":true});
            var sketch = newSketch(context, id + "F35", { "sketchPlane" : qUnion([Q0])});
            skCircle(sketch, "E204", {"center": v(72.94, 32.74) * mm, "radius": 1 * mm});
            skCircle(sketch, "E205", {"center": v(64.13, 21.7) * mm, "radius": 1 * mm});
            skSolve(sketch);
        }
        {
            var Q0;
            Q0=makeQuery(id+"F35.imprint","IMPRINT",FACE,{"disambiguationData":[TD([[makeQuery(id+"F35.imprint","IMPRINT",EDGE,{"derivedFrom":sQuery(id+"F35.wireOp",EDGE,"E204")}),1.0]])]});
            var Q1;
            Q1=makeQuery(id+"F35.imprint","IMPRINT",FACE,{"disambiguationData":[TD([[makeQuery(id+"F35.imprint","IMPRINT",EDGE,{"derivedFrom":sQuery(id+"F35.wireOp",EDGE,"E205")}),1.0]])]});
            extrude(context, id + "F36", {"entities" : qUnion([Q0, Q1]), "operationType" : NewBodyOperationType.ADD, "depth" : 25 * mm, "offsetDistance" : 25 * mm});
        }
        {
            var Q0;
            Q0=makeQuery(id+"F4.opExtrude","CAP_FACE",FACE,{"disambiguationData":[OSD([sQuery(id+"F3.wireOp",EDGE,"E22"),sQuery(id+"F3.wireOp",EDGE,"E23"),sQuery(id+"F3.wireOp",EDGE,"E24"),sQuery(id+"F3.wireOp",EDGE,"E25"),sQuery(id+"F3.wireOp",EDGE,"E26"),sQuery(id+"F3.wireOp",EDGE,"E27"),sQuery(id+"F3.wireOp",EDGE,"E28"),sQuery(id+"F3.wireOp",EDGE,"E29"),sQuery(id+"F3.wireOp",EDGE,"E30"),sQuery(id+"F3.wireOp",EDGE,"E31"),sQuery(id+"F3.wireOp",EDGE,"E32"),sQuery(id+"F3.wireOp",EDGE,"E33"),sQuery(id+"F3.wireOp",EDGE,"E34"),sQuery(id+"F3.wireOp",EDGE,"E35"),sQuery(id+"F3.wireOp",EDGE,"E36"),sQuery(id+"F3.wireOp",EDGE,"E37"),sQuery(id+"F3.wireOp",EDGE,"E38"),sQuery(id+"F3.wireOp",EDGE,"E39")])],"isStart":true});
            var sketch = newSketch(context, id + "F37", { "sketchPlane" : qUnion([Q0])});
            skCircle(sketch, "E206", {"center": v(50.52, 25) * mm, "radius": 1 * mm});
            skCircle(sketch, "E207", {"center": v(40.08, 25) * mm, "radius": 1 * mm});
            skSolve(sketch);
        }
        {
            var Q0;
            Q0=makeQuery(id+"F37.imprint","IMPRINT",FACE,{"disambiguationData":[TD([[makeQuery(id+"F37.imprint","IMPRINT",EDGE,{"derivedFrom":sQuery(id+"F37.wireOp",EDGE,"E207")}),1.0]])]});
            var Q1;
            Q1=makeQuery(id+"F37.imprint","IMPRINT",FACE,{"disambiguationData":[TD([[makeQuery(id+"F37.imprint","IMPRINT",EDGE,{"derivedFrom":sQuery(id+"F37.wireOp",EDGE,"E206")}),1.0]])]});
            extrude(context, id + "F38", {"entities" : qUnion([Q0, Q1]), "operationType" : NewBodyOperationType.ADD, "depth" : 25 * mm, "offsetDistance" : 25 * mm});
        }
        {
            var Q0;
            Q0=makeQuery(id+"F14.opPattern","COPY",BODY,{"derivedFrom":makeQuery(id+"F4.opExtrude","SWEPT_BODY",BODY,{"disambiguationData":[OSD([sQuery(id+"F3.wireOp",EDGE,"E22"),sQuery(id+"F3.wireOp",EDGE,"E23"),sQuery(id+"F3.wireOp",EDGE,"E24"),sQuery(id+"F3.wireOp",EDGE,"E25"),sQuery(id+"F3.wireOp",EDGE,"E26"),sQuery(id+"F3.wireOp",EDGE,"E27"),sQuery(id+"F3.wireOp",EDGE,"E28"),sQuery(id+"F3.wireOp",EDGE,"E29"),sQuery(id+"F3.wireOp",EDGE,"E30"),sQuery(id+"F3.wireOp",EDGE,"E31"),sQuery(id+"F3.wireOp",EDGE,"E32"),sQuery(id+"F3.wireOp",EDGE,"E33"),sQuery(id+"F3.wireOp",EDGE,"E34"),sQuery(id+"F3.wireOp",EDGE,"E35"),sQuery(id+"F3.wireOp",EDGE,"E36"),sQuery(id+"F3.wireOp",EDGE,"E37"),sQuery(id+"F3.wireOp",EDGE,"E38"),sQuery(id+"F3.wireOp",EDGE,"E39")])]}),"instanceName":"1"});
            deleteBodies(context, id + "F39", {"entities" : qUnion([Q0])});
        }
        {
            var Q0;
            Q0=makeQuery(id+"F4.opExtrude","SWEPT_BODY",BODY,{"disambiguationData":[OSD([sQuery(id+"F3.wireOp",EDGE,"E22"),sQuery(id+"F3.wireOp",EDGE,"E23"),sQuery(id+"F3.wireOp",EDGE,"E24"),sQuery(id+"F3.wireOp",EDGE,"E25"),sQuery(id+"F3.wireOp",EDGE,"E26"),sQuery(id+"F3.wireOp",EDGE,"E27"),sQuery(id+"F3.wireOp",EDGE,"E28"),sQuery(id+"F3.wireOp",EDGE,"E29"),sQuery(id+"F3.wireOp",EDGE,"E30"),sQuery(id+"F3.wireOp",EDGE,"E31"),sQuery(id+"F3.wireOp",EDGE,"E32"),sQuery(id+"F3.wireOp",EDGE,"E33"),sQuery(id+"F3.wireOp",EDGE,"E34"),sQuery(id+"F3.wireOp",EDGE,"E35"),sQuery(id+"F3.wireOp",EDGE,"E36"),sQuery(id+"F3.wireOp",EDGE,"E37"),sQuery(id+"F3.wireOp",EDGE,"E38"),sQuery(id+"F3.wireOp",EDGE,"E39")])]});
            transform(context, id + "F40", {"entities" : qUnion([Q0]), "transformType" : TransformType.TRANSLATION_3D, "dx" : 93.7 * mm, "dy" : 0 * mm, "dz" : 0 * mm, "makeCopy" : true});
        }
        {
            var Q0;
            Q0=makeQuery(id+"F6.opExtrude","CAP_FACE",FACE,{"disambiguationData":[OSD([sQuery(id+"F5.wireOp",EDGE,"E40"),sQuery(id+"F5.wireOp",EDGE,"E41"),sQuery(id+"F5.wireOp",EDGE,"E42"),sQuery(id+"F5.wireOp",EDGE,"E43"),sQuery(id+"F5.wireOp",EDGE,"E44"),sQuery(id+"F5.wireOp",EDGE,"E45"),sQuery(id+"F5.wireOp",EDGE,"E46"),sQuery(id+"F5.wireOp",EDGE,"E47"),sQuery(id+"F5.wireOp",EDGE,"E48"),sQuery(id+"F5.wireOp",EDGE,"E49"),sQuery(id+"F5.wireOp",EDGE,"E50"),sQuery(id+"F5.wireOp",EDGE,"E51"),sQuery(id+"F5.wireOp",EDGE,"E52"),sQuery(id+"F5.wireOp",EDGE,"E53")])],"isStart":true});
            var sketch = newSketch(context, id + "F41", { "sketchPlane" : qUnion([Q0])});
            skCircle(sketch, "E208", {"center": v(27.86, 31.07) * mm, "radius": 1 * mm});
            skCircle(sketch, "E209", {"center": v(27.86, 21.07) * mm, "radius": 1 * mm});
            skSolve(sketch);
        }
        {
            var Q0;
            Q0=makeQuery(id+"F41.imprint","IMPRINT",FACE,{"disambiguationData":[TD([[makeQuery(id+"F41.imprint","IMPRINT",EDGE,{"derivedFrom":sQuery(id+"F41.wireOp",EDGE,"E208")}),1.0]])]});
            var Q1;
            Q1=makeQuery(id+"F41.imprint","IMPRINT",FACE,{"disambiguationData":[TD([[makeQuery(id+"F41.imprint","IMPRINT",EDGE,{"derivedFrom":sQuery(id+"F41.wireOp",EDGE,"E209")}),1.0]])]});
            extrude(context, id + "F42", {"entities" : qUnion([Q0, Q1]), "operationType" : NewBodyOperationType.ADD, "depth" : 25 * mm, "offsetDistance" : 25 * mm});
        }
        {
            var Q0;
            Q0=makeQuery(id+"F8.opExtrude","CAP_FACE",FACE,{"disambiguationData":[OSD([sQuery(id+"F7.wireOp",EDGE,"E54"),sQuery(id+"F7.wireOp",EDGE,"E55"),sQuery(id+"F7.wireOp",EDGE,"E56"),sQuery(id+"F7.wireOp",EDGE,"E57"),sQuery(id+"F7.wireOp",EDGE,"E58"),sQuery(id+"F7.wireOp",EDGE,"E59"),sQuery(id+"F7.wireOp",EDGE,"E60"),sQuery(id+"F7.wireOp",EDGE,"E61"),sQuery(id+"F7.wireOp",EDGE,"E62"),sQuery(id+"F7.wireOp",EDGE,"E63"),sQuery(id+"F7.wireOp",EDGE,"E64"),sQuery(id+"F7.wireOp",EDGE,"E65"),sQuery(id+"F7.wireOp",EDGE,"E66"),sQuery(id+"F7.wireOp",EDGE,"E67"),sQuery(id+"F7.wireOp",EDGE,"E68"),sQuery(id+"F7.wireOp",EDGE,"E69"),sQuery(id+"F7.wireOp",EDGE,"E70"),sQuery(id+"F7.wireOp",EDGE,"E71"),sQuery(id+"F7.wireOp",EDGE,"E72"),sQuery(id+"F7.wireOp",EDGE,"E73"),sQuery(id+"F7.wireOp",EDGE,"E74"),sQuery(id+"F7.wireOp",EDGE,"E75")])],"isStart":true});
            var sketch = newSketch(context, id + "F43", { "sketchPlane" : qUnion([Q0])});
            skCircle(sketch, "E210", {"center": v(11.88, 29.08) * mm, "radius": 1 * mm});
            skCircle(sketch, "E211", {"center": v(1.01, 23.63) * mm, "radius": 1 * mm});
            skSolve(sketch);
        }
        {
            var Q0;
            Q0=makeQuery(id+"F43.imprint","IMPRINT",FACE,{"disambiguationData":[TD([[makeQuery(id+"F43.imprint","IMPRINT",EDGE,{"derivedFrom":sQuery(id+"F43.wireOp",EDGE,"E211")}),1.0]])]});
            var Q1;
            Q1=makeQuery(id+"F43.imprint","IMPRINT",FACE,{"disambiguationData":[TD([[makeQuery(id+"F43.imprint","IMPRINT",EDGE,{"derivedFrom":sQuery(id+"F43.wireOp",EDGE,"E210")}),1.0]])]});
            extrude(context, id + "F44", {"entities" : qUnion([Q0, Q1]), "operationType" : NewBodyOperationType.ADD, "depth" : 25 * mm, "offsetDistance" : 25 * mm});
        }
        {
            var Q0;
            Q0=makeQuery(id+"F15.opPattern","COPY",BODY,{"derivedFrom":makeQuery(id+"F8.opExtrude","SWEPT_BODY",BODY,{"disambiguationData":[OSD([sQuery(id+"F7.wireOp",EDGE,"E54"),sQuery(id+"F7.wireOp",EDGE,"E55"),sQuery(id+"F7.wireOp",EDGE,"E56"),sQuery(id+"F7.wireOp",EDGE,"E57"),sQuery(id+"F7.wireOp",EDGE,"E58"),sQuery(id+"F7.wireOp",EDGE,"E59"),sQuery(id+"F7.wireOp",EDGE,"E60"),sQuery(id+"F7.wireOp",EDGE,"E61"),sQuery(id+"F7.wireOp",EDGE,"E62"),sQuery(id+"F7.wireOp",EDGE,"E63"),sQuery(id+"F7.wireOp",EDGE,"E64"),sQuery(id+"F7.wireOp",EDGE,"E65"),sQuery(id+"F7.wireOp",EDGE,"E66"),sQuery(id+"F7.wireOp",EDGE,"E67"),sQuery(id+"F7.wireOp",EDGE,"E68"),sQuery(id+"F7.wireOp",EDGE,"E69"),sQuery(id+"F7.wireOp",EDGE,"E70"),sQuery(id+"F7.wireOp",EDGE,"E71"),sQuery(id+"F7.wireOp",EDGE,"E72"),sQuery(id+"F7.wireOp",EDGE,"E73"),sQuery(id+"F7.wireOp",EDGE,"E74"),sQuery(id+"F7.wireOp",EDGE,"E75")])]}),"instanceName":"1"});
            deleteBodies(context, id + "F45", {"entities" : qUnion([Q0])});
        }
        {
            var Q0;
            Q0=makeQuery(id+"F8.opExtrude","SWEPT_BODY",BODY,{"disambiguationData":[OSD([sQuery(id+"F7.wireOp",EDGE,"E54"),sQuery(id+"F7.wireOp",EDGE,"E55"),sQuery(id+"F7.wireOp",EDGE,"E56"),sQuery(id+"F7.wireOp",EDGE,"E57"),sQuery(id+"F7.wireOp",EDGE,"E58"),sQuery(id+"F7.wireOp",EDGE,"E59"),sQuery(id+"F7.wireOp",EDGE,"E60"),sQuery(id+"F7.wireOp",EDGE,"E61"),sQuery(id+"F7.wireOp",EDGE,"E62"),sQuery(id+"F7.wireOp",EDGE,"E63"),sQuery(id+"F7.wireOp",EDGE,"E64"),sQuery(id+"F7.wireOp",EDGE,"E65"),sQuery(id+"F7.wireOp",EDGE,"E66"),sQuery(id+"F7.wireOp",EDGE,"E67"),sQuery(id+"F7.wireOp",EDGE,"E68"),sQuery(id+"F7.wireOp",EDGE,"E69"),sQuery(id+"F7.wireOp",EDGE,"E70"),sQuery(id+"F7.wireOp",EDGE,"E71"),sQuery(id+"F7.wireOp",EDGE,"E72"),sQuery(id+"F7.wireOp",EDGE,"E73"),sQuery(id+"F7.wireOp",EDGE,"E74"),sQuery(id+"F7.wireOp",EDGE,"E75")])]});
            transform(context, id + "F46", {"entities" : qUnion([Q0]), "transformType" : TransformType.TRANSLATION_3D, "dx" : 79 * mm, "dy" : 0 * mm, "dz" : 0 * mm, "makeCopy" : true});
        }
        {
            var Q0;
            Q0=makeQuery(id+"F10.opExtrude","CAP_FACE",FACE,{"disambiguationData":[OSD([sQuery(id+"F9.wireOp",EDGE,"E76"),sQuery(id+"F9.wireOp",EDGE,"E77"),sQuery(id+"F9.wireOp",EDGE,"E78"),sQuery(id+"F9.wireOp",EDGE,"E79"),sQuery(id+"F9.wireOp",EDGE,"E80"),sQuery(id+"F9.wireOp",EDGE,"E81"),sQuery(id+"F9.wireOp",EDGE,"E82"),sQuery(id+"F9.wireOp",EDGE,"E83"),sQuery(id+"F9.wireOp",EDGE,"E84"),sQuery(id+"F9.wireOp",EDGE,"E85"),sQuery(id+"F9.wireOp",EDGE,"E86"),sQuery(id+"F9.wireOp",EDGE,"E87"),sQuery(id+"F9.wireOp",EDGE,"E88"),sQuery(id+"F9.wireOp",EDGE,"E89"),sQuery(id+"F9.wireOp",EDGE,"E90"),sQuery(id+"F9.wireOp",EDGE,"E91"),sQuery(id+"F9.wireOp",EDGE,"E92"),sQuery(id+"F9.wireOp",EDGE,"E93"),sQuery(id+"F9.wireOp",EDGE,"E94"),sQuery(id+"F9.wireOp",EDGE,"E95")])],"isStart":true});
            var sketch = newSketch(context, id + "F47", { "sketchPlane" : qUnion([Q0])});
            skCircle(sketch, "E212", {"center": v(-23.07, 32.74) * mm, "radius": 1 * mm});
            skCircle(sketch, "E213", {"center": v(-34.45, 22.2) * mm, "radius": 1 * mm});
            skSolve(sketch);
        }
        {
            var Q0;
            Q0=makeQuery(id+"F47.imprint","IMPRINT",FACE,{"disambiguationData":[TD([[makeQuery(id+"F47.imprint","IMPRINT",EDGE,{"derivedFrom":sQuery(id+"F47.wireOp",EDGE,"E213")}),1.0]])]});
            var Q1;
            Q1=makeQuery(id+"F47.imprint","IMPRINT",FACE,{"disambiguationData":[TD([[makeQuery(id+"F47.imprint","IMPRINT",EDGE,{"derivedFrom":sQuery(id+"F47.wireOp",EDGE,"E212")}),1.0]])]});
            extrude(context, id + "F48", {"entities" : qUnion([Q0, Q1]), "operationType" : NewBodyOperationType.ADD, "depth" : 25 * mm, "offsetDistance" : 25 * mm});
        }
        {
            var Q0;
            Q0=makeQuery(id+"F13.opExtrude","CAP_FACE",FACE,{"disambiguationData":[OSD([sQuery(id+"F12.wireOp",EDGE,"E100"),sQuery(id+"F12.wireOp",EDGE,"E101"),sQuery(id+"F12.wireOp",EDGE,"E102"),sQuery(id+"F12.wireOp",EDGE,"E103"),sQuery(id+"F12.wireOp",EDGE,"E104"),sQuery(id+"F12.wireOp",EDGE,"E105"),sQuery(id+"F12.wireOp",EDGE,"E106"),sQuery(id+"F12.wireOp",EDGE,"E107"),sQuery(id+"F12.wireOp",EDGE,"E108"),sQuery(id+"F12.wireOp",EDGE,"E109"),sQuery(id+"F12.wireOp",EDGE,"E110"),sQuery(id+"F12.wireOp",EDGE,"E111"),sQuery(id+"F12.wireOp",EDGE,"E112"),sQuery(id+"F12.wireOp",EDGE,"E113"),sQuery(id+"F12.wireOp",EDGE,"E114.trimOffspring")])],"isStart":true});
            var sketch = newSketch(context, id + "F49", { "sketchPlane" : qUnion([Q0])});
            skCircle(sketch, "E214", {"center": v(-99.16, 26.96) * mm, "radius": 1 * mm});
            skCircle(sketch, "E215", {"center": v(-88.6, 21.23) * mm, "radius": 1 * mm});
            skPoint(sketch, "E215.centerSnap0", {"position": v(-90.19, 21.23) * mm});
            skSolve(sketch);
        }
        {
            var Q0;
            Q0=makeQuery(id+"F49.imprint","IMPRINT",FACE,{"disambiguationData":[TD([[makeQuery(id+"F49.imprint","IMPRINT",EDGE,{"derivedFrom":sQuery(id+"F49.wireOp",EDGE,"E214")}),1.0]])]});
            var Q1;
            Q1=makeQuery(id+"F49.imprint","IMPRINT",FACE,{"disambiguationData":[TD([[makeQuery(id+"F49.imprint","IMPRINT",EDGE,{"derivedFrom":sQuery(id+"F49.wireOp",EDGE,"E215")}),1.0]])]});
            extrude(context, id + "F50", {"entities" : qUnion([Q0, Q1]), "operationType" : NewBodyOperationType.ADD, "depth" : 25 * mm, "offsetDistance" : 25 * mm});
        }
        {
            var Q0;
            Q0=makeQuery(id+"F13.opExtrude","CAP_FACE",FACE,{"disambiguationData":[OSD([sQuery(id+"F12.wireOp",EDGE,"E96"),sQuery(id+"F12.wireOp",EDGE,"E97"),sQuery(id+"F12.wireOp",EDGE,"E98"),sQuery(id+"F12.wireOp",EDGE,"E99")])],"isStart":true});
            var sketch = newSketch(context, id + "F51", { "sketchPlane" : qUnion([Q0])});
            skCircle(sketch, "E216", {"center": v(-95.2, 38.58) * mm, "radius": 1 * mm});
            skSolve(sketch);
        }
        {
            var Q0;
            Q0=makeQuery(id+"F51.imprint","IMPRINT",FACE,{"disambiguationData":[TD([[makeQuery(id+"F51.imprint","IMPRINT",EDGE,{"derivedFrom":sQuery(id+"F51.wireOp",EDGE,"E216")}),1.0]])]});
            extrude(context, id + "F52", {"entities" : qUnion([Q0]), "operationType" : NewBodyOperationType.ADD, "depth" : 25 * mm, "offsetDistance" : 25 * mm});
        }
        {
            var Q0;
            Q0=makeQuery(id+"F17.opExtrude","CAP_FACE",FACE,{"disambiguationData":[OSD([sQuery(id+"F16.wireOp",EDGE,"E116"),sQuery(id+"F16.wireOp",EDGE,"E117"),sQuery(id+"F16.wireOp",EDGE,"E118"),sQuery(id+"F16.wireOp",EDGE,"E119"),sQuery(id+"F16.wireOp",EDGE,"E120"),sQuery(id+"F16.wireOp",EDGE,"E121"),sQuery(id+"F16.wireOp",EDGE,"E122"),sQuery(id+"F16.wireOp",EDGE,"E123"),sQuery(id+"F16.wireOp",EDGE,"E124"),sQuery(id+"F16.wireOp",EDGE,"E125"),sQuery(id+"F16.wireOp",EDGE,"E126"),sQuery(id+"F16.wireOp",EDGE,"E127")])],"isStart":true});
            var sketch = newSketch(context, id + "F53", { "sketchPlane" : qUnion([Q0])});
            skCircle(sketch, "E217", {"center": v(40.34, -17.7) * mm, "radius": 1 * mm});
            skCircle(sketch, "E218", {"center": v(40.34, -28.15) * mm, "radius": 1 * mm});
            skSolve(sketch);
        }
        {
            var Q0;
            Q0=makeQuery(id+"F53.imprint","IMPRINT",FACE,{"disambiguationData":[TD([[makeQuery(id+"F53.imprint","IMPRINT",EDGE,{"derivedFrom":sQuery(id+"F53.wireOp",EDGE,"E217")}),1.0]])]});
            var Q1;
            Q1=makeQuery(id+"F53.imprint","IMPRINT",FACE,{"disambiguationData":[TD([[makeQuery(id+"F53.imprint","IMPRINT",EDGE,{"derivedFrom":sQuery(id+"F53.wireOp",EDGE,"E218")}),1.0]])]});
            extrude(context, id + "F54", {"entities" : qUnion([Q0, Q1]), "operationType" : NewBodyOperationType.ADD, "depth" : 25 * mm, "offsetDistance" : 25 * mm});
        }
        {
            var Q0;
            Q0=makeQuery(id+"F18.opPattern","COPY",BODY,{"derivedFrom":makeQuery(id+"F17.opExtrude","SWEPT_BODY",BODY,{"disambiguationData":[OSD([sQuery(id+"F16.wireOp",EDGE,"E116"),sQuery(id+"F16.wireOp",EDGE,"E117"),sQuery(id+"F16.wireOp",EDGE,"E118"),sQuery(id+"F16.wireOp",EDGE,"E119"),sQuery(id+"F16.wireOp",EDGE,"E120"),sQuery(id+"F16.wireOp",EDGE,"E121"),sQuery(id+"F16.wireOp",EDGE,"E122"),sQuery(id+"F16.wireOp",EDGE,"E123"),sQuery(id+"F16.wireOp",EDGE,"E124"),sQuery(id+"F16.wireOp",EDGE,"E125"),sQuery(id+"F16.wireOp",EDGE,"E126"),sQuery(id+"F16.wireOp",EDGE,"E127")])]}),"instanceName":"1"});
            deleteBodies(context, id + "F55", {"entities" : qUnion([Q0])});
        }
        {
            var Q0;
            Q0=makeQuery(id+"F17.opExtrude","SWEPT_BODY",BODY,{"disambiguationData":[OSD([sQuery(id+"F16.wireOp",EDGE,"E116"),sQuery(id+"F16.wireOp",EDGE,"E117"),sQuery(id+"F16.wireOp",EDGE,"E118"),sQuery(id+"F16.wireOp",EDGE,"E119"),sQuery(id+"F16.wireOp",EDGE,"E120"),sQuery(id+"F16.wireOp",EDGE,"E121"),sQuery(id+"F16.wireOp",EDGE,"E122"),sQuery(id+"F16.wireOp",EDGE,"E123"),sQuery(id+"F16.wireOp",EDGE,"E124"),sQuery(id+"F16.wireOp",EDGE,"E125"),sQuery(id+"F16.wireOp",EDGE,"E126"),sQuery(id+"F16.wireOp",EDGE,"E127")])]});
            transform(context, id + "F56", {"entities" : qUnion([Q0]), "transformType" : TransformType.TRANSLATION_3D, "dx" : 103.4 * mm, "dy" : 0 * mm, "dz" : 0 * mm, "makeCopy" : true});
        }
        {
            var Q0;
            Q0=makeQuery(id+"F26.opExtrude","CAP_FACE",FACE,{"disambiguationData":[OSD([sQuery(id+"F25.wireOp",EDGE,"E154"),sQuery(id+"F25.wireOp",EDGE,"E155"),sQuery(id+"F25.wireOp",EDGE,"E156"),sQuery(id+"F25.wireOp",EDGE,"E157"),sQuery(id+"F25.wireOp",EDGE,"E158"),sQuery(id+"F25.wireOp",EDGE,"E159"),sQuery(id+"F25.wireOp",EDGE,"E160"),sQuery(id+"F25.wireOp",EDGE,"E161"),sQuery(id+"F25.wireOp",EDGE,"E162"),sQuery(id+"F25.wireOp",EDGE,"E163"),sQuery(id+"F25.wireOp",EDGE,"E164"),sQuery(id+"F25.wireOp",EDGE,"E167"),sQuery(id+"F25.wireOp",EDGE,"E168"),sQuery(id+"F25.wireOp",EDGE,"E169"),sQuery(id+"F25.wireOp",EDGE,"E170"),sQuery(id+"F25.wireOp",EDGE,"E171.trimOffspring")])],"isStart":true});
            var sketch = newSketch(context, id + "F57", { "sketchPlane" : qUnion([Q0])});
            skCircle(sketch, "E219", {"center": v(32.84, -22.6) * mm, "radius": 1 * mm});
            skPoint(sketch, "E219.centerSnap0", {"position": v(34.09, -22.6) * mm});
            skCircle(sketch, "E220", {"center": v(23.43, -23.05) * mm, "radius": 1 * mm});
            skSolve(sketch);
        }
        {
            var Q0;
            Q0=makeQuery(id+"F57.imprint","IMPRINT",FACE,{"disambiguationData":[TD([[makeQuery(id+"F57.imprint","IMPRINT",EDGE,{"derivedFrom":sQuery(id+"F57.wireOp",EDGE,"E220")}),1.0]])]});
            var Q1;
            Q1=makeQuery(id+"F57.imprint","IMPRINT",FACE,{"disambiguationData":[TD([[makeQuery(id+"F57.imprint","IMPRINT",EDGE,{"derivedFrom":sQuery(id+"F57.wireOp",EDGE,"E219")}),1.0]])]});
            extrude(context, id + "F58", {"entities" : qUnion([Q0, Q1]), "operationType" : NewBodyOperationType.ADD, "depth" : 25 * mm, "offsetDistance" : 25 * mm});
        }
        {
            var Q0;
            Q0=makeQuery(id+"F28.opExtrude","CAP_FACE",FACE,{"disambiguationData":[OSD([sQuery(id+"F27.wireOp",EDGE,"E173"),sQuery(id+"F27.wireOp",EDGE,"E174"),sQuery(id+"F27.wireOp",EDGE,"E175"),sQuery(id+"F27.wireOp",EDGE,"E176"),sQuery(id+"F27.wireOp",EDGE,"E177"),sQuery(id+"F27.wireOp",EDGE,"E178"),sQuery(id+"F27.wireOp",EDGE,"E179"),sQuery(id+"F27.wireOp",EDGE,"E180"),sQuery(id+"F27.wireOp",EDGE,"E181"),sQuery(id+"F27.wireOp",EDGE,"E182"),sQuery(id+"F27.wireOp",EDGE,"E183"),sQuery(id+"F27.wireOp",EDGE,"E184"),sQuery(id+"F27.wireOp",EDGE,"E185"),sQuery(id+"F27.wireOp",EDGE,"E186"),sQuery(id+"F27.wireOp",EDGE,"E187"),sQuery(id+"F27.wireOp",EDGE,"E188"),sQuery(id+"F27.wireOp",EDGE,"E189")])],"isStart":true});
            var sketch = newSketch(context, id + "F59", { "sketchPlane" : qUnion([Q0])});
            skCircle(sketch, "E221", {"center": v(11.36, -19.12) * mm, "radius": 1 * mm});
            skPoint(sketch, "E221.centerSnap0", {"position": v(10.12, -19.12) * mm});
            skCircle(sketch, "E222", {"center": v(10.5, -30.06) * mm, "radius": 1 * mm});
            skSolve(sketch);
        }
        {
            var Q0;
            Q0=makeQuery(id+"F59.imprint","IMPRINT",FACE,{"disambiguationData":[TD([[makeQuery(id+"F59.imprint","IMPRINT",EDGE,{"derivedFrom":sQuery(id+"F59.wireOp",EDGE,"E221")}),1.0]])]});
            var Q1;
            Q1=makeQuery(id+"F59.imprint","IMPRINT",FACE,{"disambiguationData":[TD([[makeQuery(id+"F59.imprint","IMPRINT",EDGE,{"derivedFrom":sQuery(id+"F59.wireOp",EDGE,"E222")}),1.0]])]});
            extrude(context, id + "F60", {"entities" : qUnion([Q0, Q1]), "operationType" : NewBodyOperationType.ADD, "depth" : 25 * mm, "offsetDistance" : 25 * mm});
        }
        {
            var Q0;
            Q0=makeQuery(id+"F20.opExtrude","CAP_FACE",FACE,{"disambiguationData":[OSD([sQuery(id+"F19.wireOp",EDGE,"E128"),sQuery(id+"F19.wireOp",EDGE,"E129"),sQuery(id+"F19.wireOp",EDGE,"E130"),sQuery(id+"F19.wireOp",EDGE,"E131"),sQuery(id+"F19.wireOp",EDGE,"E132"),sQuery(id+"F19.wireOp",EDGE,"E133"),sQuery(id+"F19.wireOp",EDGE,"E134"),sQuery(id+"F19.wireOp",EDGE,"E135"),sQuery(id+"F19.wireOp",EDGE,"E136"),sQuery(id+"F19.wireOp",EDGE,"E137"),sQuery(id+"F19.wireOp",EDGE,"E138.trimOffspring"),sQuery(id+"F19.wireOp",EDGE,"E139.trimOffspring"),sQuery(id+"F19.wireOp",EDGE,"E140.trimOffspring"),sQuery(id+"F19.wireOp",EDGE,"E141.trimOffspring")])],"isStart":true});
            var sketch = newSketch(context, id + "F61", { "sketchPlane" : qUnion([Q0])});
            skCircle(sketch, "E223", {"center": v(-2.6, -17.5) * mm, "radius": 1 * mm});
            skCircle(sketch, "E224", {"center": v(-2.85, -28.58) * mm, "radius": 1 * mm});
            skSolve(sketch);
        }
        {
            var Q0;
            Q0=makeQuery(id+"F61.imprint","IMPRINT",FACE,{"disambiguationData":[TD([[makeQuery(id+"F61.imprint","IMPRINT",EDGE,{"derivedFrom":sQuery(id+"F61.wireOp",EDGE,"E223")}),1.0]])]});
            var Q1;
            Q1=makeQuery(id+"F61.imprint","IMPRINT",FACE,{"disambiguationData":[TD([[makeQuery(id+"F61.imprint","IMPRINT",EDGE,{"derivedFrom":sQuery(id+"F61.wireOp",EDGE,"E224")}),1.0]])]});
            extrude(context, id + "F62", {"entities" : qUnion([Q0, Q1]), "operationType" : NewBodyOperationType.ADD, "depth" : 25 * mm, "offsetDistance" : 25 * mm});
        }
        {
            var Q0;
            Q0=makeQuery(id+"F30.opExtrude","CAP_FACE",FACE,{"disambiguationData":[OSD([sQuery(id+"F29.wireOp",EDGE,"E190.bottom"),sQuery(id+"F29.wireOp",EDGE,"E190.top"),sQuery(id+"F29.wireOp",EDGE,"E190.left"),sQuery(id+"F29.wireOp",EDGE,"E190.right")])],"isStart":true});
            var sketch = newSketch(context, id + "F63", { "sketchPlane" : qUnion([Q0])});
            skCircle(sketch, "E225", {"center": v(-20.47, -22.28) * mm, "radius": 1 * mm});
            skCircle(sketch, "E226", {"center": v(-15.86, -22.28) * mm, "radius": 1 * mm});
            skSolve(sketch);
        }
        {
            var Q0;
            Q0=makeQuery(id+"F63.imprint","IMPRINT",FACE,{"disambiguationData":[TD([[makeQuery(id+"F63.imprint","IMPRINT",EDGE,{"derivedFrom":sQuery(id+"F63.wireOp",EDGE,"E225")}),1.0]])]});
            var Q1;
            Q1=makeQuery(id+"F63.imprint","IMPRINT",FACE,{"disambiguationData":[TD([[makeQuery(id+"F63.imprint","IMPRINT",EDGE,{"derivedFrom":sQuery(id+"F63.wireOp",EDGE,"E226")}),1.0]])]});
            extrude(context, id + "F64", {"entities" : qUnion([Q0, Q1]), "operationType" : NewBodyOperationType.ADD, "depth" : 25 * mm, "offsetDistance" : 25 * mm});
        }
        {
            var Q0;
            Q0=makeQuery(id+"F32.opExtrude","CAP_FACE",FACE,{"disambiguationData":[OSD([sQuery(id+"F31.wireOp",EDGE,"E191"),sQuery(id+"F31.wireOp",EDGE,"E192"),sQuery(id+"F31.wireOp",EDGE,"E193"),sQuery(id+"F31.wireOp",EDGE,"E194"),sQuery(id+"F31.wireOp",EDGE,"E195"),sQuery(id+"F31.wireOp",EDGE,"E196"),sQuery(id+"F31.wireOp",EDGE,"E197"),sQuery(id+"F31.wireOp",EDGE,"E198"),sQuery(id+"F31.wireOp",EDGE,"E199"),sQuery(id+"F31.wireOp",EDGE,"E200"),sQuery(id+"F31.wireOp",EDGE,"E201"),sQuery(id+"F31.wireOp",EDGE,"E202"),sQuery(id+"F31.wireOp",EDGE,"E203")])],"isStart":true});
            var sketch = newSketch(context, id + "F65", { "sketchPlane" : qUnion([Q0])});
            skCircle(sketch, "E227", {"center": v(-40.1, -18.9) * mm, "radius": 1 * mm});
            skCircle(sketch, "E228", {"center": v(-33.77, -28.2) * mm, "radius": 1 * mm});
            skSolve(sketch);
        }
        {
            var Q0;
            Q0=makeQuery(id+"F65.imprint","IMPRINT",FACE,{"disambiguationData":[TD([[makeQuery(id+"F65.imprint","IMPRINT",EDGE,{"derivedFrom":sQuery(id+"F65.wireOp",EDGE,"E228")}),1.0]])]});
            var Q1;
            Q1=makeQuery(id+"F65.imprint","IMPRINT",FACE,{"disambiguationData":[TD([[makeQuery(id+"F65.imprint","IMPRINT",EDGE,{"derivedFrom":sQuery(id+"F65.wireOp",EDGE,"E227")}),1.0]])]});
            extrude(context, id + "F66", {"entities" : qUnion([Q0, Q1]), "operationType" : NewBodyOperationType.ADD, "depth" : 25 * mm, "offsetDistance" : 25 * mm});
        }
        {
            var Q0;
            Q0=makeQuery(id+"F24.opExtrude","CAP_FACE",FACE,{"disambiguationData":[OSD([sQuery(id+"F23.wireOp",EDGE,"E149"),sQuery(id+"F23.wireOp",EDGE,"E150"),sQuery(id+"F23.wireOp",EDGE,"E151"),sQuery(id+"F23.wireOp",EDGE,"E152"),sQuery(id+"F23.wireOp",EDGE,"E153")])],"isStart":true});
            var sketch = newSketch(context, id + "F67", { "sketchPlane" : qUnion([Q0])});
            skCircle(sketch, "E229", {"center": v(-56.82, -22.75) * mm, "radius": 1 * mm});
            skCircle(sketch, "E230", {"center": v(-45.3, -22.75) * mm, "radius": 1 * mm});
            skPoint(sketch, "E230.centerSnap0", {"position": v(-46.43, -22.75) * mm});
            skSolve(sketch);
        }
        {
            var Q0;
            Q0=makeQuery(id+"F67.imprint","IMPRINT",FACE,{"disambiguationData":[TD([[makeQuery(id+"F67.imprint","IMPRINT",EDGE,{"derivedFrom":sQuery(id+"F67.wireOp",EDGE,"E229")}),1.0]])]});
            var Q1;
            Q1=makeQuery(id+"F67.imprint","IMPRINT",FACE,{"disambiguationData":[TD([[makeQuery(id+"F67.imprint","IMPRINT",EDGE,{"derivedFrom":sQuery(id+"F67.wireOp",EDGE,"E230")}),1.0]])]});
            extrude(context, id + "F68", {"entities" : qUnion([Q0, Q1]), "operationType" : NewBodyOperationType.ADD, "depth" : 25 * mm, "offsetDistance" : 25 * mm});
        }
        {
            var Q0;
            Q0=makeQuery(id+"F22.opExtrude","CAP_FACE",FACE,{"disambiguationData":[OSD([sQuery(id+"F21.wireOp",EDGE,"E142"),sQuery(id+"F21.wireOp",EDGE,"E143"),sQuery(id+"F21.wireOp",EDGE,"E144"),sQuery(id+"F21.wireOp",EDGE,"E145"),sQuery(id+"F21.wireOp",EDGE,"E146"),sQuery(id+"F21.wireOp",EDGE,"E147"),sQuery(id+"F21.wireOp",EDGE,"E148")])],"isStart":true});
            var sketch = newSketch(context, id + "F69", { "sketchPlane" : qUnion([Q0])});
            skCircle(sketch, "E231", {"center": v(-78.12, -17.6) * mm, "radius": 1 * mm});
            skCircle(sketch, "E232", {"center": v(-72.45, -31.7) * mm, "radius": 1 * mm});
            skSolve(sketch);
        }
        {
            var Q0;
            Q0=makeQuery(id+"F69.imprint","IMPRINT",FACE,{"disambiguationData":[TD([[makeQuery(id+"F69.imprint","IMPRINT",EDGE,{"derivedFrom":sQuery(id+"F69.wireOp",EDGE,"E231")}),1.0]])]});
            var Q1;
            {var subQ0=sQuery(id+"F69.wireOp",EDGE,"E232");var subQ1=makeQuery(id+"F22.opExtrude","CAP_EDGE",EDGE,{"disambiguationData":[OSD([sQuery(id+"F21.wireOp",EDGE,"E148")])],"isStart":true});var subQ2=makeQuery(id+"F69.imprint","INTERSECT",VERTEX,{"disambiguationData":[OD(0.0)],"derivedFrom":[subQ1,subQ0]});Q1=makeQuery(id+"F69.imprint","IMPRINT",FACE,{"disambiguationData":[TD([[makeQuery(id+"F69.imprint","IMPRINT",EDGE,{"disambiguationData":[TD([[subQ2,1.0]])],"derivedFrom":subQ0}),1.0]])]});}
            extrude(context, id + "F70", {"entities" : qUnion([Q0, Q1]), "operationType" : NewBodyOperationType.ADD, "depth" : 25 * mm, "offsetDistance" : 25 * mm});
        }
        {
            var Q0;
            Q0=makeQuery(id+"F4.opExtrude","SWEPT_BODY",BODY,{"disambiguationData":[OSD([sQuery(id+"F3.wireOp",EDGE,"E22"),sQuery(id+"F3.wireOp",EDGE,"E23"),sQuery(id+"F3.wireOp",EDGE,"E24"),sQuery(id+"F3.wireOp",EDGE,"E25"),sQuery(id+"F3.wireOp",EDGE,"E26"),sQuery(id+"F3.wireOp",EDGE,"E27"),sQuery(id+"F3.wireOp",EDGE,"E28"),sQuery(id+"F3.wireOp",EDGE,"E29"),sQuery(id+"F3.wireOp",EDGE,"E30"),sQuery(id+"F3.wireOp",EDGE,"E31"),sQuery(id+"F3.wireOp",EDGE,"E32"),sQuery(id+"F3.wireOp",EDGE,"E33"),sQuery(id+"F3.wireOp",EDGE,"E34"),sQuery(id+"F3.wireOp",EDGE,"E35"),sQuery(id+"F3.wireOp",EDGE,"E36"),sQuery(id+"F3.wireOp",EDGE,"E37"),sQuery(id+"F3.wireOp",EDGE,"E38"),sQuery(id+"F3.wireOp",EDGE,"E39")])]});
            var Q1;
            Q1=makeQuery(id+"F4.opExtrude","SWEPT_EDGE",EDGE,{"disambiguationData":[OSD([sQuery(id+"F3.wireOp",EDGE,"E25"),sQuery(id+"F3.wireOp",EDGE,"E26")])]});
            transform(context, id + "F71", {"entities" : qUnion([Q0]), "transformType" : TransformType.ROTATION, "transformAxis" : qUnion([Q1]), "angle" : 90 * degree, "makeCopy" : false});
        }
        {
            var Q0;
            Q0=makeQuery(id+"F4.opExtrude","SWEPT_BODY",BODY,{"disambiguationData":[OSD([sQuery(id+"F3.wireOp",EDGE,"E22"),sQuery(id+"F3.wireOp",EDGE,"E23"),sQuery(id+"F3.wireOp",EDGE,"E24"),sQuery(id+"F3.wireOp",EDGE,"E25"),sQuery(id+"F3.wireOp",EDGE,"E26"),sQuery(id+"F3.wireOp",EDGE,"E27"),sQuery(id+"F3.wireOp",EDGE,"E28"),sQuery(id+"F3.wireOp",EDGE,"E29"),sQuery(id+"F3.wireOp",EDGE,"E30"),sQuery(id+"F3.wireOp",EDGE,"E31"),sQuery(id+"F3.wireOp",EDGE,"E32"),sQuery(id+"F3.wireOp",EDGE,"E33"),sQuery(id+"F3.wireOp",EDGE,"E34"),sQuery(id+"F3.wireOp",EDGE,"E35"),sQuery(id+"F3.wireOp",EDGE,"E36"),sQuery(id+"F3.wireOp",EDGE,"E37"),sQuery(id+"F3.wireOp",EDGE,"E38"),sQuery(id+"F3.wireOp",EDGE,"E39")])]});
            transform(context, id + "F72", {"entities" : qUnion([Q0]), "transformType" : TransformType.TRANSLATION_3D, "dx" : -38.2 * mm, "dy" : 0 * mm, "dz" : -12.7 * mm, "makeCopy" : false});
        }
        {
            var Q0;
            Q0=makeQuery(id+"F8.opExtrude","SWEPT_BODY",BODY,{"disambiguationData":[OSD([sQuery(id+"F7.wireOp",EDGE,"E54"),sQuery(id+"F7.wireOp",EDGE,"E55"),sQuery(id+"F7.wireOp",EDGE,"E56"),sQuery(id+"F7.wireOp",EDGE,"E57"),sQuery(id+"F7.wireOp",EDGE,"E58"),sQuery(id+"F7.wireOp",EDGE,"E59"),sQuery(id+"F7.wireOp",EDGE,"E60"),sQuery(id+"F7.wireOp",EDGE,"E61"),sQuery(id+"F7.wireOp",EDGE,"E62"),sQuery(id+"F7.wireOp",EDGE,"E63"),sQuery(id+"F7.wireOp",EDGE,"E64"),sQuery(id+"F7.wireOp",EDGE,"E65"),sQuery(id+"F7.wireOp",EDGE,"E66"),sQuery(id+"F7.wireOp",EDGE,"E67"),sQuery(id+"F7.wireOp",EDGE,"E68"),sQuery(id+"F7.wireOp",EDGE,"E69"),sQuery(id+"F7.wireOp",EDGE,"E70"),sQuery(id+"F7.wireOp",EDGE,"E71"),sQuery(id+"F7.wireOp",EDGE,"E72"),sQuery(id+"F7.wireOp",EDGE,"E73"),sQuery(id+"F7.wireOp",EDGE,"E74"),sQuery(id+"F7.wireOp",EDGE,"E75")])]});
            var Q1;
            Q1=makeQuery(id+"F8.opExtrude","SWEPT_EDGE",EDGE,{"disambiguationData":[OSD([sQuery(id+"F7.wireOp",EDGE,"E63"),sQuery(id+"F7.wireOp",EDGE,"E64")])]});
            transform(context, id + "F73", {"entities" : qUnion([Q0]), "transformType" : TransformType.ROTATION, "transformAxis" : qUnion([Q1]), "angle" : 90 * degree, "oppositeDirection" : true, "makeCopy" : false});
        }
        {
            var Q0;
            Q0=makeQuery(id+"F8.opExtrude","SWEPT_BODY",BODY,{"disambiguationData":[OSD([sQuery(id+"F7.wireOp",EDGE,"E54"),sQuery(id+"F7.wireOp",EDGE,"E55"),sQuery(id+"F7.wireOp",EDGE,"E56"),sQuery(id+"F7.wireOp",EDGE,"E57"),sQuery(id+"F7.wireOp",EDGE,"E58"),sQuery(id+"F7.wireOp",EDGE,"E59"),sQuery(id+"F7.wireOp",EDGE,"E60"),sQuery(id+"F7.wireOp",EDGE,"E61"),sQuery(id+"F7.wireOp",EDGE,"E62"),sQuery(id+"F7.wireOp",EDGE,"E63"),sQuery(id+"F7.wireOp",EDGE,"E64"),sQuery(id+"F7.wireOp",EDGE,"E65"),sQuery(id+"F7.wireOp",EDGE,"E66"),sQuery(id+"F7.wireOp",EDGE,"E67"),sQuery(id+"F7.wireOp",EDGE,"E68"),sQuery(id+"F7.wireOp",EDGE,"E69"),sQuery(id+"F7.wireOp",EDGE,"E70"),sQuery(id+"F7.wireOp",EDGE,"E71"),sQuery(id+"F7.wireOp",EDGE,"E72"),sQuery(id+"F7.wireOp",EDGE,"E73"),sQuery(id+"F7.wireOp",EDGE,"E74"),sQuery(id+"F7.wireOp",EDGE,"E75")])]});
            transform(context, id + "F74", {"entities" : qUnion([Q0]), "transformType" : TransformType.TRANSLATION_3D, "dx" : -66.7 * mm, "dy" : 0 * mm, "dz" : -3.1 * mm, "makeCopy" : false});
        }
        {
            var Q0;
            Q0=makeQuery(id+"F6.opExtrude","SWEPT_BODY",BODY,{"disambiguationData":[OSD([sQuery(id+"F5.wireOp",EDGE,"E40"),sQuery(id+"F5.wireOp",EDGE,"E41"),sQuery(id+"F5.wireOp",EDGE,"E42"),sQuery(id+"F5.wireOp",EDGE,"E43"),sQuery(id+"F5.wireOp",EDGE,"E44"),sQuery(id+"F5.wireOp",EDGE,"E45"),sQuery(id+"F5.wireOp",EDGE,"E46"),sQuery(id+"F5.wireOp",EDGE,"E47"),sQuery(id+"F5.wireOp",EDGE,"E48"),sQuery(id+"F5.wireOp",EDGE,"E49"),sQuery(id+"F5.wireOp",EDGE,"E50"),sQuery(id+"F5.wireOp",EDGE,"E51"),sQuery(id+"F5.wireOp",EDGE,"E52"),sQuery(id+"F5.wireOp",EDGE,"E53")])]});
            var Q1;
            Q1=makeQuery(id+"F6.opExtrude","SWEPT_EDGE",EDGE,{"disambiguationData":[OSD([sQuery(id+"F5.wireOp",EDGE,"E40"),sQuery(id+"F5.wireOp",EDGE,"E46")])]});
            transform(context, id + "F75", {"entities" : qUnion([Q0]), "transformType" : TransformType.ROTATION, "transformAxis" : qUnion([Q1]), "angle" : 35 * degree, "makeCopy" : false});
        }
        {
            var Q0;
            Q0=makeQuery(id+"F6.opExtrude","SWEPT_BODY",BODY,{"disambiguationData":[OSD([sQuery(id+"F5.wireOp",EDGE,"E40"),sQuery(id+"F5.wireOp",EDGE,"E41"),sQuery(id+"F5.wireOp",EDGE,"E42"),sQuery(id+"F5.wireOp",EDGE,"E43"),sQuery(id+"F5.wireOp",EDGE,"E44"),sQuery(id+"F5.wireOp",EDGE,"E45"),sQuery(id+"F5.wireOp",EDGE,"E46"),sQuery(id+"F5.wireOp",EDGE,"E47"),sQuery(id+"F5.wireOp",EDGE,"E48"),sQuery(id+"F5.wireOp",EDGE,"E49"),sQuery(id+"F5.wireOp",EDGE,"E50"),sQuery(id+"F5.wireOp",EDGE,"E51"),sQuery(id+"F5.wireOp",EDGE,"E52"),sQuery(id+"F5.wireOp",EDGE,"E53")])]});
            transform(context, id + "F76", {"entities" : qUnion([Q0]), "transformType" : TransformType.TRANSLATION_3D, "dx" : -57.5 * mm, "dy" : 0 * mm, "dz" : 17.2 * mm, "makeCopy" : false});
        }
        {
            var Q0;
            Q0=makeQuery(id+"F40.opPattern","COPY",BODY,{"derivedFrom":makeQuery(id+"F4.opExtrude","SWEPT_BODY",BODY,{"disambiguationData":[OSD([sQuery(id+"F3.wireOp",EDGE,"E22"),sQuery(id+"F3.wireOp",EDGE,"E23"),sQuery(id+"F3.wireOp",EDGE,"E24"),sQuery(id+"F3.wireOp",EDGE,"E25"),sQuery(id+"F3.wireOp",EDGE,"E26"),sQuery(id+"F3.wireOp",EDGE,"E27"),sQuery(id+"F3.wireOp",EDGE,"E28"),sQuery(id+"F3.wireOp",EDGE,"E29"),sQuery(id+"F3.wireOp",EDGE,"E30"),sQuery(id+"F3.wireOp",EDGE,"E31"),sQuery(id+"F3.wireOp",EDGE,"E32"),sQuery(id+"F3.wireOp",EDGE,"E33"),sQuery(id+"F3.wireOp",EDGE,"E34"),sQuery(id+"F3.wireOp",EDGE,"E35"),sQuery(id+"F3.wireOp",EDGE,"E36"),sQuery(id+"F3.wireOp",EDGE,"E37"),sQuery(id+"F3.wireOp",EDGE,"E38"),sQuery(id+"F3.wireOp",EDGE,"E39")])]}),"instanceName":"1"});
            var Q1;
            Q1=makeQuery(id+"F40.opPattern","COPY",EDGE,{"derivedFrom":makeQuery(id+"F4.opExtrude","SWEPT_EDGE",EDGE,{"disambiguationData":[OSD([sQuery(id+"F3.wireOp",EDGE,"E36"),sQuery(id+"F3.wireOp",EDGE,"E37")])]}),"instanceName":"1"});
            transform(context, id + "F77", {"entities" : qUnion([Q0]), "transformType" : TransformType.ROTATION, "transformAxis" : qUnion([Q1]), "angle" : 90 * degree, "makeCopy" : false});
        }
        {
            var Q0;
            Q0=makeQuery(id+"F40.opPattern","COPY",BODY,{"derivedFrom":makeQuery(id+"F4.opExtrude","SWEPT_BODY",BODY,{"disambiguationData":[OSD([sQuery(id+"F3.wireOp",EDGE,"E22"),sQuery(id+"F3.wireOp",EDGE,"E23"),sQuery(id+"F3.wireOp",EDGE,"E24"),sQuery(id+"F3.wireOp",EDGE,"E25"),sQuery(id+"F3.wireOp",EDGE,"E26"),sQuery(id+"F3.wireOp",EDGE,"E27"),sQuery(id+"F3.wireOp",EDGE,"E28"),sQuery(id+"F3.wireOp",EDGE,"E29"),sQuery(id+"F3.wireOp",EDGE,"E30"),sQuery(id+"F3.wireOp",EDGE,"E31"),sQuery(id+"F3.wireOp",EDGE,"E32"),sQuery(id+"F3.wireOp",EDGE,"E33"),sQuery(id+"F3.wireOp",EDGE,"E34"),sQuery(id+"F3.wireOp",EDGE,"E35"),sQuery(id+"F3.wireOp",EDGE,"E36"),sQuery(id+"F3.wireOp",EDGE,"E37"),sQuery(id+"F3.wireOp",EDGE,"E38"),sQuery(id+"F3.wireOp",EDGE,"E39")])]}),"instanceName":"1"});
            transform(context, id + "F78", {"entities" : qUnion([Q0]), "transformType" : TransformType.TRANSLATION_3D, "dx" : -26.2 * mm, "dy" : 0 * mm, "dz" : -2.1 * mm, "makeCopy" : false});
        }
        {
            var Q0;
            Q0=makeQuery(id+"F13.opExtrude","SWEPT_BODY",BODY,{"disambiguationData":[OSD([sQuery(id+"F12.wireOp",EDGE,"E100"),sQuery(id+"F12.wireOp",EDGE,"E101"),sQuery(id+"F12.wireOp",EDGE,"E102"),sQuery(id+"F12.wireOp",EDGE,"E103"),sQuery(id+"F12.wireOp",EDGE,"E104"),sQuery(id+"F12.wireOp",EDGE,"E105"),sQuery(id+"F12.wireOp",EDGE,"E106"),sQuery(id+"F12.wireOp",EDGE,"E107"),sQuery(id+"F12.wireOp",EDGE,"E108"),sQuery(id+"F12.wireOp",EDGE,"E109"),sQuery(id+"F12.wireOp",EDGE,"E110"),sQuery(id+"F12.wireOp",EDGE,"E111"),sQuery(id+"F12.wireOp",EDGE,"E112"),sQuery(id+"F12.wireOp",EDGE,"E113"),sQuery(id+"F12.wireOp",EDGE,"E114.trimOffspring")])]});
            var Q1;
            Q1=makeQuery(id+"F13.opExtrude","SWEPT_EDGE",EDGE,{"disambiguationData":[OSD([sQuery(id+"F12.wireOp",EDGE,"E106"),sQuery(id+"F12.wireOp",EDGE,"E107")])]});
            transform(context, id + "F79", {"entities" : qUnion([Q0]), "transformType" : TransformType.ROTATION, "transformAxis" : qUnion([Q1]), "angle" : 90 * degree, "makeCopy" : false});
        }
        {
            var Q0;
            Q0=makeQuery(id+"F13.opExtrude","SWEPT_BODY",BODY,{"disambiguationData":[OSD([sQuery(id+"F12.wireOp",EDGE,"E100"),sQuery(id+"F12.wireOp",EDGE,"E101"),sQuery(id+"F12.wireOp",EDGE,"E102"),sQuery(id+"F12.wireOp",EDGE,"E103"),sQuery(id+"F12.wireOp",EDGE,"E104"),sQuery(id+"F12.wireOp",EDGE,"E105"),sQuery(id+"F12.wireOp",EDGE,"E106"),sQuery(id+"F12.wireOp",EDGE,"E107"),sQuery(id+"F12.wireOp",EDGE,"E108"),sQuery(id+"F12.wireOp",EDGE,"E109"),sQuery(id+"F12.wireOp",EDGE,"E110"),sQuery(id+"F12.wireOp",EDGE,"E111"),sQuery(id+"F12.wireOp",EDGE,"E112"),sQuery(id+"F12.wireOp",EDGE,"E113"),sQuery(id+"F12.wireOp",EDGE,"E114.trimOffspring")])]});
            transform(context, id + "F80", {"entities" : qUnion([Q0]), "transformType" : TransformType.TRANSLATION_3D, "dx" : -77.6 * mm, "dy" : 0 * mm, "dz" : 21.8 * mm, "makeCopy" : false});
        }
        {
            var Q0;
            Q0=makeQuery(id+"F46.opPattern","COPY",BODY,{"derivedFrom":makeQuery(id+"F8.opExtrude","SWEPT_BODY",BODY,{"disambiguationData":[OSD([sQuery(id+"F7.wireOp",EDGE,"E54"),sQuery(id+"F7.wireOp",EDGE,"E55"),sQuery(id+"F7.wireOp",EDGE,"E56"),sQuery(id+"F7.wireOp",EDGE,"E57"),sQuery(id+"F7.wireOp",EDGE,"E58"),sQuery(id+"F7.wireOp",EDGE,"E59"),sQuery(id+"F7.wireOp",EDGE,"E60"),sQuery(id+"F7.wireOp",EDGE,"E61"),sQuery(id+"F7.wireOp",EDGE,"E62"),sQuery(id+"F7.wireOp",EDGE,"E63"),sQuery(id+"F7.wireOp",EDGE,"E64"),sQuery(id+"F7.wireOp",EDGE,"E65"),sQuery(id+"F7.wireOp",EDGE,"E66"),sQuery(id+"F7.wireOp",EDGE,"E67"),sQuery(id+"F7.wireOp",EDGE,"E68"),sQuery(id+"F7.wireOp",EDGE,"E69"),sQuery(id+"F7.wireOp",EDGE,"E70"),sQuery(id+"F7.wireOp",EDGE,"E71"),sQuery(id+"F7.wireOp",EDGE,"E72"),sQuery(id+"F7.wireOp",EDGE,"E73"),sQuery(id+"F7.wireOp",EDGE,"E74"),sQuery(id+"F7.wireOp",EDGE,"E75")])]}),"instanceName":"1"});
            var Q1;
            Q1=makeQuery(id+"F46.opPattern","COPY",EDGE,{"derivedFrom":makeQuery(id+"F8.opExtrude","SWEPT_EDGE",EDGE,{"disambiguationData":[OSD([sQuery(id+"F7.wireOp",EDGE,"E64"),sQuery(id+"F7.wireOp",EDGE,"E65")])]}),"instanceName":"1"});
            transform(context, id + "F81", {"entities" : qUnion([Q0]), "transformType" : TransformType.ROTATION, "transformAxis" : qUnion([Q1]), "angle" : 90 * degree, "makeCopy" : false});
        }
        {
            var Q0;
            Q0=makeQuery(id+"F46.opPattern","COPY",BODY,{"derivedFrom":makeQuery(id+"F8.opExtrude","SWEPT_BODY",BODY,{"disambiguationData":[OSD([sQuery(id+"F7.wireOp",EDGE,"E54"),sQuery(id+"F7.wireOp",EDGE,"E55"),sQuery(id+"F7.wireOp",EDGE,"E56"),sQuery(id+"F7.wireOp",EDGE,"E57"),sQuery(id+"F7.wireOp",EDGE,"E58"),sQuery(id+"F7.wireOp",EDGE,"E59"),sQuery(id+"F7.wireOp",EDGE,"E60"),sQuery(id+"F7.wireOp",EDGE,"E61"),sQuery(id+"F7.wireOp",EDGE,"E62"),sQuery(id+"F7.wireOp",EDGE,"E63"),sQuery(id+"F7.wireOp",EDGE,"E64"),sQuery(id+"F7.wireOp",EDGE,"E65"),sQuery(id+"F7.wireOp",EDGE,"E66"),sQuery(id+"F7.wireOp",EDGE,"E67"),sQuery(id+"F7.wireOp",EDGE,"E68"),sQuery(id+"F7.wireOp",EDGE,"E69"),sQuery(id+"F7.wireOp",EDGE,"E70"),sQuery(id+"F7.wireOp",EDGE,"E71"),sQuery(id+"F7.wireOp",EDGE,"E72"),sQuery(id+"F7.wireOp",EDGE,"E73"),sQuery(id+"F7.wireOp",EDGE,"E74"),sQuery(id+"F7.wireOp",EDGE,"E75")])]}),"instanceName":"1"});
            transform(context, id + "F82", {"entities" : qUnion([Q0]), "transformType" : TransformType.TRANSLATION_3D, "dx" : -38.7 * mm, "dy" : 0 * mm, "dz" : 19 * mm, "makeCopy" : false});
        }
        {
            var Q0;
            Q0=makeQuery(id+"F24.opExtrude","SWEPT_BODY",BODY,{"disambiguationData":[OSD([sQuery(id+"F23.wireOp",EDGE,"E149"),sQuery(id+"F23.wireOp",EDGE,"E150"),sQuery(id+"F23.wireOp",EDGE,"E151"),sQuery(id+"F23.wireOp",EDGE,"E152"),sQuery(id+"F23.wireOp",EDGE,"E153")])]});
            transform(context, id + "F83", {"entities" : qUnion([Q0]), "transformType" : TransformType.TRANSLATION_3D, "dx" : -42 * mm, "dy" : 0 * mm, "dz" : 64.7 * mm, "makeCopy" : false});
        }
        {
            var Q0;
            Q0=makeQuery(id+"F13.opExtrude","SWEPT_BODY",BODY,{"disambiguationData":[OSD([sQuery(id+"F12.wireOp",EDGE,"E96"),sQuery(id+"F12.wireOp",EDGE,"E97"),sQuery(id+"F12.wireOp",EDGE,"E98"),sQuery(id+"F12.wireOp",EDGE,"E99")])]});
            transform(context, id + "F84", {"entities" : qUnion([Q0]), "transformType" : TransformType.TRANSLATION_3D, "dx" : -63.8 * mm, "dy" : 0 * mm, "dz" : 20.7 * mm, "makeCopy" : false});
        }
        {
            var Q0;
            Q0=makeQuery(id+"F13.opExtrude","SWEPT_BODY",BODY,{"disambiguationData":[OSD([sQuery(id+"F12.wireOp",EDGE,"E96"),sQuery(id+"F12.wireOp",EDGE,"E97"),sQuery(id+"F12.wireOp",EDGE,"E98"),sQuery(id+"F12.wireOp",EDGE,"E99")])]});
            var Q1;
            Q1=makeQuery(id+"F13.opExtrude","SWEPT_EDGE",EDGE,{"disambiguationData":[OSD([sQuery(id+"F12.wireOp",EDGE,"E97"),sQuery(id+"F12.wireOp",EDGE,"E98")])]});
            transform(context, id + "F85", {"entities" : qUnion([Q0]), "transformType" : TransformType.ROTATION, "transformAxis" : qUnion([Q1]), "angle" : 50 * degree, "makeCopy" : false});
        }
        {
            var Q0;
            Q0=makeQuery(id+"F13.opExtrude","SWEPT_BODY",BODY,{"disambiguationData":[OSD([sQuery(id+"F12.wireOp",EDGE,"E96"),sQuery(id+"F12.wireOp",EDGE,"E97"),sQuery(id+"F12.wireOp",EDGE,"E98"),sQuery(id+"F12.wireOp",EDGE,"E99")])]});
            transform(context, id + "F86", {"entities" : qUnion([Q0]), "transformType" : TransformType.TRANSLATION_3D, "dx" : -1.3 * mm, "dy" : 0 * mm, "dz" : -4.6 * mm, "makeCopy" : false});
        }
        {
            var Q0;
            Q0=makeQuery(id+"F30.opExtrude","SWEPT_BODY",BODY,{"disambiguationData":[OSD([sQuery(id+"F29.wireOp",EDGE,"E190.bottom"),sQuery(id+"F29.wireOp",EDGE,"E190.top"),sQuery(id+"F29.wireOp",EDGE,"E190.left"),sQuery(id+"F29.wireOp",EDGE,"E190.right")])]});
            transform(context, id + "F87", {"entities" : qUnion([Q0]), "transformType" : TransformType.TRANSLATION_3D, "dx" : -84.3 * mm, "dy" : 0 * mm, "dz" : 71.1 * mm, "makeCopy" : false});
        }
        {
            var Q0;
            Q0=makeQuery(id+"F32.opExtrude","SWEPT_BODY",BODY,{"disambiguationData":[OSD([sQuery(id+"F31.wireOp",EDGE,"E191"),sQuery(id+"F31.wireOp",EDGE,"E192"),sQuery(id+"F31.wireOp",EDGE,"E193"),sQuery(id+"F31.wireOp",EDGE,"E194"),sQuery(id+"F31.wireOp",EDGE,"E195"),sQuery(id+"F31.wireOp",EDGE,"E196"),sQuery(id+"F31.wireOp",EDGE,"E197"),sQuery(id+"F31.wireOp",EDGE,"E198"),sQuery(id+"F31.wireOp",EDGE,"E199"),sQuery(id+"F31.wireOp",EDGE,"E200"),sQuery(id+"F31.wireOp",EDGE,"E201"),sQuery(id+"F31.wireOp",EDGE,"E202"),sQuery(id+"F31.wireOp",EDGE,"E203")])]});
            var Q1;
            Q1=makeQuery(id+"F32.opExtrude","SWEPT_EDGE",EDGE,{"disambiguationData":[OSD([sQuery(id+"F31.wireOp",EDGE,"E192"),sQuery(id+"F31.wireOp",EDGE,"E193")])]});
            transform(context, id + "F88", {"entities" : qUnion([Q0]), "transformType" : TransformType.ROTATION, "transformAxis" : qUnion([Q1]), "angle" : 180 * degree, "makeCopy" : false});
        }
        {
            var Q0;
            Q0=makeQuery(id+"F32.opExtrude","SWEPT_BODY",BODY,{"disambiguationData":[OSD([sQuery(id+"F31.wireOp",EDGE,"E191"),sQuery(id+"F31.wireOp",EDGE,"E192"),sQuery(id+"F31.wireOp",EDGE,"E193"),sQuery(id+"F31.wireOp",EDGE,"E194"),sQuery(id+"F31.wireOp",EDGE,"E195"),sQuery(id+"F31.wireOp",EDGE,"E196"),sQuery(id+"F31.wireOp",EDGE,"E197"),sQuery(id+"F31.wireOp",EDGE,"E198"),sQuery(id+"F31.wireOp",EDGE,"E199"),sQuery(id+"F31.wireOp",EDGE,"E200"),sQuery(id+"F31.wireOp",EDGE,"E201"),sQuery(id+"F31.wireOp",EDGE,"E202"),sQuery(id+"F31.wireOp",EDGE,"E203")])]});
            transform(context, id + "F89", {"entities" : qUnion([Q0]), "transformType" : TransformType.TRANSLATION_3D, "dx" : -82 * mm, "dy" : 0 * mm, "dz" : -0.3 * mm, "makeCopy" : false});
        }
        {
            var Q0;
            Q0=makeQuery(id+"F17.opExtrude","SWEPT_BODY",BODY,{"disambiguationData":[OSD([sQuery(id+"F16.wireOp",EDGE,"E116"),sQuery(id+"F16.wireOp",EDGE,"E117"),sQuery(id+"F16.wireOp",EDGE,"E118"),sQuery(id+"F16.wireOp",EDGE,"E119"),sQuery(id+"F16.wireOp",EDGE,"E120"),sQuery(id+"F16.wireOp",EDGE,"E121"),sQuery(id+"F16.wireOp",EDGE,"E122"),sQuery(id+"F16.wireOp",EDGE,"E123"),sQuery(id+"F16.wireOp",EDGE,"E124"),sQuery(id+"F16.wireOp",EDGE,"E125"),sQuery(id+"F16.wireOp",EDGE,"E126"),sQuery(id+"F16.wireOp",EDGE,"E127")])]});
            transform(context, id + "F90", {"entities" : qUnion([Q0]), "transformType" : TransformType.TRANSLATION_3D, "dx" : 22.6 * mm, "dy" : 0 * mm, "dz" : 0 * mm, "makeCopy" : false});
        }
        {
            var Q0;
            Q0=makeQuery(id+"F28.opExtrude","SWEPT_BODY",BODY,{"disambiguationData":[OSD([sQuery(id+"F27.wireOp",EDGE,"E173"),sQuery(id+"F27.wireOp",EDGE,"E174"),sQuery(id+"F27.wireOp",EDGE,"E175"),sQuery(id+"F27.wireOp",EDGE,"E176"),sQuery(id+"F27.wireOp",EDGE,"E177"),sQuery(id+"F27.wireOp",EDGE,"E178"),sQuery(id+"F27.wireOp",EDGE,"E179"),sQuery(id+"F27.wireOp",EDGE,"E180"),sQuery(id+"F27.wireOp",EDGE,"E181"),sQuery(id+"F27.wireOp",EDGE,"E182"),sQuery(id+"F27.wireOp",EDGE,"E183"),sQuery(id+"F27.wireOp",EDGE,"E184"),sQuery(id+"F27.wireOp",EDGE,"E185"),sQuery(id+"F27.wireOp",EDGE,"E186"),sQuery(id+"F27.wireOp",EDGE,"E187"),sQuery(id+"F27.wireOp",EDGE,"E188"),sQuery(id+"F27.wireOp",EDGE,"E189")])]});
            var Q1;
            Q1=makeQuery(id+"F28.opExtrude","SWEPT_EDGE",EDGE,{"disambiguationData":[OSD([sQuery(id+"F27.wireOp",EDGE,"E175"),sQuery(id+"F27.wireOp",EDGE,"E188")])]});
            transform(context, id + "F91", {"entities" : qUnion([Q0]), "transformType" : TransformType.ROTATION, "transformAxis" : qUnion([Q1]), "angle" : 180 * degree, "makeCopy" : false});
        }
        {
            var Q0;
            Q0=makeQuery(id+"F28.opExtrude","SWEPT_BODY",BODY,{"disambiguationData":[OSD([sQuery(id+"F27.wireOp",EDGE,"E173"),sQuery(id+"F27.wireOp",EDGE,"E174"),sQuery(id+"F27.wireOp",EDGE,"E175"),sQuery(id+"F27.wireOp",EDGE,"E176"),sQuery(id+"F27.wireOp",EDGE,"E177"),sQuery(id+"F27.wireOp",EDGE,"E178"),sQuery(id+"F27.wireOp",EDGE,"E179"),sQuery(id+"F27.wireOp",EDGE,"E180"),sQuery(id+"F27.wireOp",EDGE,"E181"),sQuery(id+"F27.wireOp",EDGE,"E182"),sQuery(id+"F27.wireOp",EDGE,"E183"),sQuery(id+"F27.wireOp",EDGE,"E184"),sQuery(id+"F27.wireOp",EDGE,"E185"),sQuery(id+"F27.wireOp",EDGE,"E186"),sQuery(id+"F27.wireOp",EDGE,"E187"),sQuery(id+"F27.wireOp",EDGE,"E188"),sQuery(id+"F27.wireOp",EDGE,"E189")])]});
            transform(context, id + "F92", {"entities" : qUnion([Q0]), "transformType" : TransformType.TRANSLATION_3D, "dx" : -20.6 * mm, "dy" : 0 * mm, "dz" : 14.1 * mm, "makeCopy" : false});
        }
        {
            var Q0;
            Q0=makeQuery(id+"F22.opExtrude","SWEPT_BODY",BODY,{"disambiguationData":[OSD([sQuery(id+"F21.wireOp",EDGE,"E142"),sQuery(id+"F21.wireOp",EDGE,"E143"),sQuery(id+"F21.wireOp",EDGE,"E144"),sQuery(id+"F21.wireOp",EDGE,"E145"),sQuery(id+"F21.wireOp",EDGE,"E146"),sQuery(id+"F21.wireOp",EDGE,"E147"),sQuery(id+"F21.wireOp",EDGE,"E148")])]});
            transform(context, id + "F93", {"entities" : qUnion([Q0]), "transformType" : TransformType.TRANSLATION_3D, "dx" : -110.6 * mm, "dy" : 0 * mm, "dz" : 7 * mm, "makeCopy" : false});
        }
        {
            var Q0;
            Q0=makeQuery(id+"F56.opPattern","COPY",BODY,{"derivedFrom":makeQuery(id+"F17.opExtrude","SWEPT_BODY",BODY,{"disambiguationData":[OSD([sQuery(id+"F16.wireOp",EDGE,"E116"),sQuery(id+"F16.wireOp",EDGE,"E117"),sQuery(id+"F16.wireOp",EDGE,"E118"),sQuery(id+"F16.wireOp",EDGE,"E119"),sQuery(id+"F16.wireOp",EDGE,"E120"),sQuery(id+"F16.wireOp",EDGE,"E121"),sQuery(id+"F16.wireOp",EDGE,"E122"),sQuery(id+"F16.wireOp",EDGE,"E123"),sQuery(id+"F16.wireOp",EDGE,"E124"),sQuery(id+"F16.wireOp",EDGE,"E125"),sQuery(id+"F16.wireOp",EDGE,"E126"),sQuery(id+"F16.wireOp",EDGE,"E127")])]}),"instanceName":"1"});
            var Q1;
            Q1=makeQuery(id+"F56.opPattern","COPY",EDGE,{"derivedFrom":makeQuery(id+"F17.opExtrude","SWEPT_EDGE",EDGE,{"disambiguationData":[OSD([sQuery(id+"F16.wireOp",EDGE,"E121"),sQuery(id+"F16.wireOp",EDGE,"E122")])]}),"instanceName":"1"});
            transform(context, id + "F94", {"entities" : qUnion([Q0]), "transformType" : TransformType.ROTATION, "transformAxis" : qUnion([Q1]), "angle" : 90 * degree, "makeCopy" : false});
        }
        {
            var Q0;
            Q0=makeQuery(id+"F56.opPattern","COPY",BODY,{"derivedFrom":makeQuery(id+"F17.opExtrude","SWEPT_BODY",BODY,{"disambiguationData":[OSD([sQuery(id+"F16.wireOp",EDGE,"E116"),sQuery(id+"F16.wireOp",EDGE,"E117"),sQuery(id+"F16.wireOp",EDGE,"E118"),sQuery(id+"F16.wireOp",EDGE,"E119"),sQuery(id+"F16.wireOp",EDGE,"E120"),sQuery(id+"F16.wireOp",EDGE,"E121"),sQuery(id+"F16.wireOp",EDGE,"E122"),sQuery(id+"F16.wireOp",EDGE,"E123"),sQuery(id+"F16.wireOp",EDGE,"E124"),sQuery(id+"F16.wireOp",EDGE,"E125"),sQuery(id+"F16.wireOp",EDGE,"E126"),sQuery(id+"F16.wireOp",EDGE,"E127")])]}),"instanceName":"1"});
            transform(context, id + "F95", {"entities" : qUnion([Q0]), "transformType" : TransformType.TRANSLATION_3D, "dx" : -80.9 * mm, "dy" : 0 * mm, "dz" : 1.3 * mm, "makeCopy" : false});
        }
        {
            var Q0;
            Q0=makeQuery(id+"F20.opExtrude","SWEPT_BODY",BODY,{"disambiguationData":[OSD([sQuery(id+"F19.wireOp",EDGE,"E128"),sQuery(id+"F19.wireOp",EDGE,"E129"),sQuery(id+"F19.wireOp",EDGE,"E130"),sQuery(id+"F19.wireOp",EDGE,"E131"),sQuery(id+"F19.wireOp",EDGE,"E132"),sQuery(id+"F19.wireOp",EDGE,"E133"),sQuery(id+"F19.wireOp",EDGE,"E134"),sQuery(id+"F19.wireOp",EDGE,"E135"),sQuery(id+"F19.wireOp",EDGE,"E136"),sQuery(id+"F19.wireOp",EDGE,"E137"),sQuery(id+"F19.wireOp",EDGE,"E138.trimOffspring"),sQuery(id+"F19.wireOp",EDGE,"E139.trimOffspring"),sQuery(id+"F19.wireOp",EDGE,"E140.trimOffspring"),sQuery(id+"F19.wireOp",EDGE,"E141.trimOffspring")])]});
            var Q1;
            Q1=makeQuery(id+"F20.opExtrude","SWEPT_EDGE",EDGE,{"disambiguationData":[OSD([sQuery(id+"F19.wireOp",EDGE,"E129"),sQuery(id+"F19.wireOp",EDGE,"E141.trimOffspring")])]});
            transform(context, id + "F96", {"entities" : qUnion([Q0]), "transformType" : TransformType.ROTATION, "transformAxis" : qUnion([Q1]), "angle" : 20 * degree, "makeCopy" : false});
        }
        {
            var Q0;
            Q0=makeQuery(id+"F20.opExtrude","SWEPT_BODY",BODY,{"disambiguationData":[OSD([sQuery(id+"F19.wireOp",EDGE,"E128"),sQuery(id+"F19.wireOp",EDGE,"E129"),sQuery(id+"F19.wireOp",EDGE,"E130"),sQuery(id+"F19.wireOp",EDGE,"E131"),sQuery(id+"F19.wireOp",EDGE,"E132"),sQuery(id+"F19.wireOp",EDGE,"E133"),sQuery(id+"F19.wireOp",EDGE,"E134"),sQuery(id+"F19.wireOp",EDGE,"E135"),sQuery(id+"F19.wireOp",EDGE,"E136"),sQuery(id+"F19.wireOp",EDGE,"E137"),sQuery(id+"F19.wireOp",EDGE,"E138.trimOffspring"),sQuery(id+"F19.wireOp",EDGE,"E139.trimOffspring"),sQuery(id+"F19.wireOp",EDGE,"E140.trimOffspring"),sQuery(id+"F19.wireOp",EDGE,"E141.trimOffspring")])]});
            transform(context, id + "F97", {"entities" : qUnion([Q0]), "transformType" : TransformType.TRANSLATION_3D, "dx" : -23.5 * mm, "dy" : 0 * mm, "dz" : -15.7 * mm, "makeCopy" : false});
        }
        {
            var Q0;
            Q0=qCreatedBy(makeId("Front.planeOp"),FACE);
            cPlane(context, id + "F98", {"entities" : qUnion([Q0]), "cplaneType" : CPlaneType.OFFSET, "offset" : 24 * mm, "oppositeDirection" : true, "width" : 150 * mm, "height" : 150 * mm});
        }
        {
            var Q0;
            Q0=qCreatedBy(id+"F98.planeOp",FACE);
            var sketch = newSketch(context, id + "F99", { "sketchPlane" : qUnion([Q0])});
            skLineSegment(sketch, "E233", {"start": v(-65.36, 53.63) * mm, "end": v(-67.48, 48.52) * mm});
            skLineSegment(sketch, "E234", {"start": v(-67.48, 48.52) * mm, "end": v(-70.8, 43.08) * mm});
            skLineSegment(sketch, "E235", {"start": v(-70.8, 43.08) * mm, "end": v(-71.96, 32.83) * mm});
            skLineSegment(sketch, "E236", {"start": v(-71.96, 32.83) * mm, "end": v(-73, 31.71) * mm});
            skLineSegment(sketch, "E237", {"start": v(-73, 31.71) * mm, "end": v(-83.34, 30.76) * mm});
            skLineSegment(sketch, "E238", {"start": v(-83.34, 30.76) * mm, "end": v(-83.51, 32.65) * mm});
            skLineSegment(sketch, "E239", {"start": v(-83.51, 32.65) * mm, "end": v(-73.53, 33.58) * mm});
            skLineSegment(sketch, "E240", {"start": v(-73.53, 33.58) * mm, "end": v(-72.67, 42.8) * mm});
            skLineSegment(sketch, "E241", {"start": v(-72.67, 42.8) * mm, "end": v(-85.12, 51.84) * mm});
            skLineSegment(sketch, "E242", {"start": v(-85.12, 51.84) * mm, "end": v(-84.07, 53.29) * mm});
            skLineSegment(sketch, "E243", {"start": v(-84.07, 53.29) * mm, "end": v(-72, 44.52) * mm});
            skLineSegment(sketch, "E244", {"start": v(-72, 44.52) * mm, "end": v(-69.35, 49.35) * mm});
            skLineSegment(sketch, "E245", {"start": v(-69.35, 49.35) * mm, "end": v(-67.2, 54.42) * mm});
            skLineSegment(sketch, "E246", {"start": v(-67.2, 54.42) * mm, "end": v(-65.36, 53.63) * mm});
            skSolve(sketch);
        }
        {
            var Q0;
            Q0=makeQuery(id+"F99.imprint","IMPRINT",FACE,{"disambiguationData":[TD([[makeQuery(id+"F99.imprint","IMPRINT",EDGE,{"derivedFrom":sQuery(id+"F99.wireOp",EDGE,"E233")}),-1.0]])]});
            extrude(context, id + "F100", {"entities" : qUnion([Q0]), "operationType" : NewBodyOperationType.ADD, "oppositeDirection" : true, "depth" : 1 * mm, "offsetDistance" : 25 * mm});
        }
        {
            var Q0;
            Q0=qCreatedBy(id+"F98.planeOp",FACE);
            var sketch = newSketch(context, id + "F101", { "sketchPlane" : qUnion([Q0])});
            skLineSegment(sketch, "E247", {"start": v(30.82, 59.29) * mm, "end": v(31.48, 43.44) * mm});
            skLineSegment(sketch, "E248", {"start": v(31.48, 43.44) * mm, "end": v(31.48, 42.34) * mm});
            skLineSegment(sketch, "E249", {"start": v(31.48, 42.34) * mm, "end": v(23.9, 32.09) * mm});
            skLineSegment(sketch, "E250", {"start": v(23.9, 32.09) * mm, "end": v(12.26, 30.87) * mm});
            skLineSegment(sketch, "E251", {"start": v(12.26, 30.87) * mm, "end": v(10.99, 31.31) * mm});
            skLineSegment(sketch, "E252", {"start": v(10.99, 31.31) * mm, "end": v(13.81, 42.17) * mm});
            skLineSegment(sketch, "E253", {"start": v(13.81, 42.17) * mm, "end": v(9.21, 53.03) * mm});
            skLineSegment(sketch, "E254", {"start": v(24.5, 54.74) * mm, "end": v(28.83, 59.68) * mm});
            skLineSegment(sketch, "E255", {"start": v(28.83, 59.68) * mm, "end": v(30.82, 59.29) * mm});
            skLineSegment(sketch, "E256", {"start": v(29.32, 58.12) * mm, "end": v(25.11, 52.8) * mm});
            skLineSegment(sketch, "E257", {"start": v(25.11, 52.8) * mm, "end": v(11.15, 52.8) * mm});
            skLineSegment(sketch, "E258", {"start": v(11.15, 52.8) * mm, "end": v(15.64, 42.5) * mm});
            skLineSegment(sketch, "E259", {"start": v(15.64, 42.5) * mm, "end": v(12.7, 32.64) * mm});
            skLineSegment(sketch, "E260", {"start": v(12.7, 32.64) * mm, "end": v(22.79, 33.58) * mm});
            skLineSegment(sketch, "E261", {"start": v(22.79, 33.58) * mm, "end": v(29.66, 43.44) * mm});
            skLineSegment(sketch, "E262", {"start": v(29.66, 43.44) * mm, "end": v(29.32, 58.12) * mm});
            skLineSegment(sketch, "E263", {"start": v(24.5, 54.74) * mm, "end": v(10.16, 54.2) * mm});
            skLineSegment(sketch, "E264", {"start": v(10.16, 54.2) * mm, "end": v(9.21, 53.03) * mm});
            skSolve(sketch);
        }
        {
            var Q0;
            Q0=makeQuery(id+"F101.imprint","IMPRINT",FACE,{"disambiguationData":[TD([[makeQuery(id+"F101.imprint","IMPRINT",EDGE,{"derivedFrom":sQuery(id+"F101.wireOp",EDGE,"E247")}),-1.0]])]});
            extrude(context, id + "F102", {"entities" : qUnion([Q0]), "operationType" : NewBodyOperationType.ADD, "oppositeDirection" : true, "depth" : 1 * mm, "offsetDistance" : 25 * mm});
        }
        {
            var Q0;
            Q0=qCreatedBy(id+"F98.planeOp",FACE);
            var sketch = newSketch(context, id + "F103", { "sketchPlane" : qUnion([Q0])});
            skLineSegment(sketch, "E265", {"start": v(-14.34, -33.08) * mm, "end": v(-16.98, -27.58) * mm});
            skLineSegment(sketch, "E266", {"start": v(-16.98, -27.58) * mm, "end": v(-22.7, -22.48) * mm});
            skLineSegment(sketch, "E267", {"start": v(-22.7, -22.48) * mm, "end": v(-24.72, -11.36) * mm});
            skLineSegment(sketch, "E268", {"start": v(-32.26, -9.65) * mm, "end": v(-33.1, -11.36) * mm});
            skLineSegment(sketch, "E269", {"start": v(-33.1, -11.36) * mm, "end": v(-33.87, -22.33) * mm});
            skLineSegment(sketch, "E270", {"start": v(-33.87, -22.33) * mm, "end": v(-38.41, -23.77) * mm});
            skLineSegment(sketch, "E271", {"start": v(-38.41, -23.77) * mm, "end": v(-47.55, -20.73) * mm});
            skLineSegment(sketch, "E272", {"start": v(-47.55, -20.73) * mm, "end": v(-48.66, -22.44) * mm});
            skLineSegment(sketch, "E273", {"start": v(-48.66, -22.44) * mm, "end": v(-38.58, -25.6) * mm});
            skLineSegment(sketch, "E274", {"start": v(-38.58, -25.6) * mm, "end": v(-33.2, -31.59) * mm});
            skLineSegment(sketch, "E275", {"start": v(-33.2, -31.59) * mm, "end": v(-31.78, -30.3) * mm});
            skLineSegment(sketch, "E276", {"start": v(-31.78, -30.3) * mm, "end": v(-36.23, -25.36) * mm});
            skLineSegment(sketch, "E277", {"start": v(-32.54, -23.5) * mm, "end": v(-31.93, -22.28) * mm});
            skLineSegment(sketch, "E278", {"start": v(-31.93, -22.28) * mm, "end": v(-31.32, -11.48) * mm});
            skLineSegment(sketch, "E279", {"start": v(-31.32, -11.48) * mm, "end": v(-26.33, -12.25) * mm});
            skLineSegment(sketch, "E280", {"start": v(-26.33, -12.25) * mm, "end": v(-24.45, -23.28) * mm});
            skLineSegment(sketch, "E281", {"start": v(-24.45, -23.28) * mm, "end": v(-18.41, -28.76) * mm});
            skLineSegment(sketch, "E282", {"start": v(-18.41, -28.76) * mm, "end": v(-16.03, -33.86) * mm});
            skLineSegment(sketch, "E283", {"start": v(-16.03, -33.86) * mm, "end": v(-14.34, -33.08) * mm});
            skLineSegment(sketch, "E284", {"start": v(-32.54, -23.5) * mm, "end": v(-36.23, -25.36) * mm});
            skLineSegment(sketch, "E285", {"start": v(-24.72, -11.36) * mm, "end": v(-25.48, -10.5) * mm});
            skLineSegment(sketch, "E286", {"start": v(-25.48, -10.5) * mm, "end": v(-32.26, -9.65) * mm});
            skSolve(sketch);
        }
        {
            var Q0;
            Q0=makeQuery(id+"F103.imprint","IMPRINT",FACE,{"disambiguationData":[TD([[makeQuery(id+"F103.imprint","IMPRINT",EDGE,{"derivedFrom":sQuery(id+"F103.wireOp",EDGE,"E265")}),1.0]])]});
            extrude(context, id + "F104", {"entities" : qUnion([Q0]), "operationType" : NewBodyOperationType.ADD, "oppositeDirection" : true, "depth" : 1 * mm, "offsetDistance" : 25 * mm});
        }
    });
